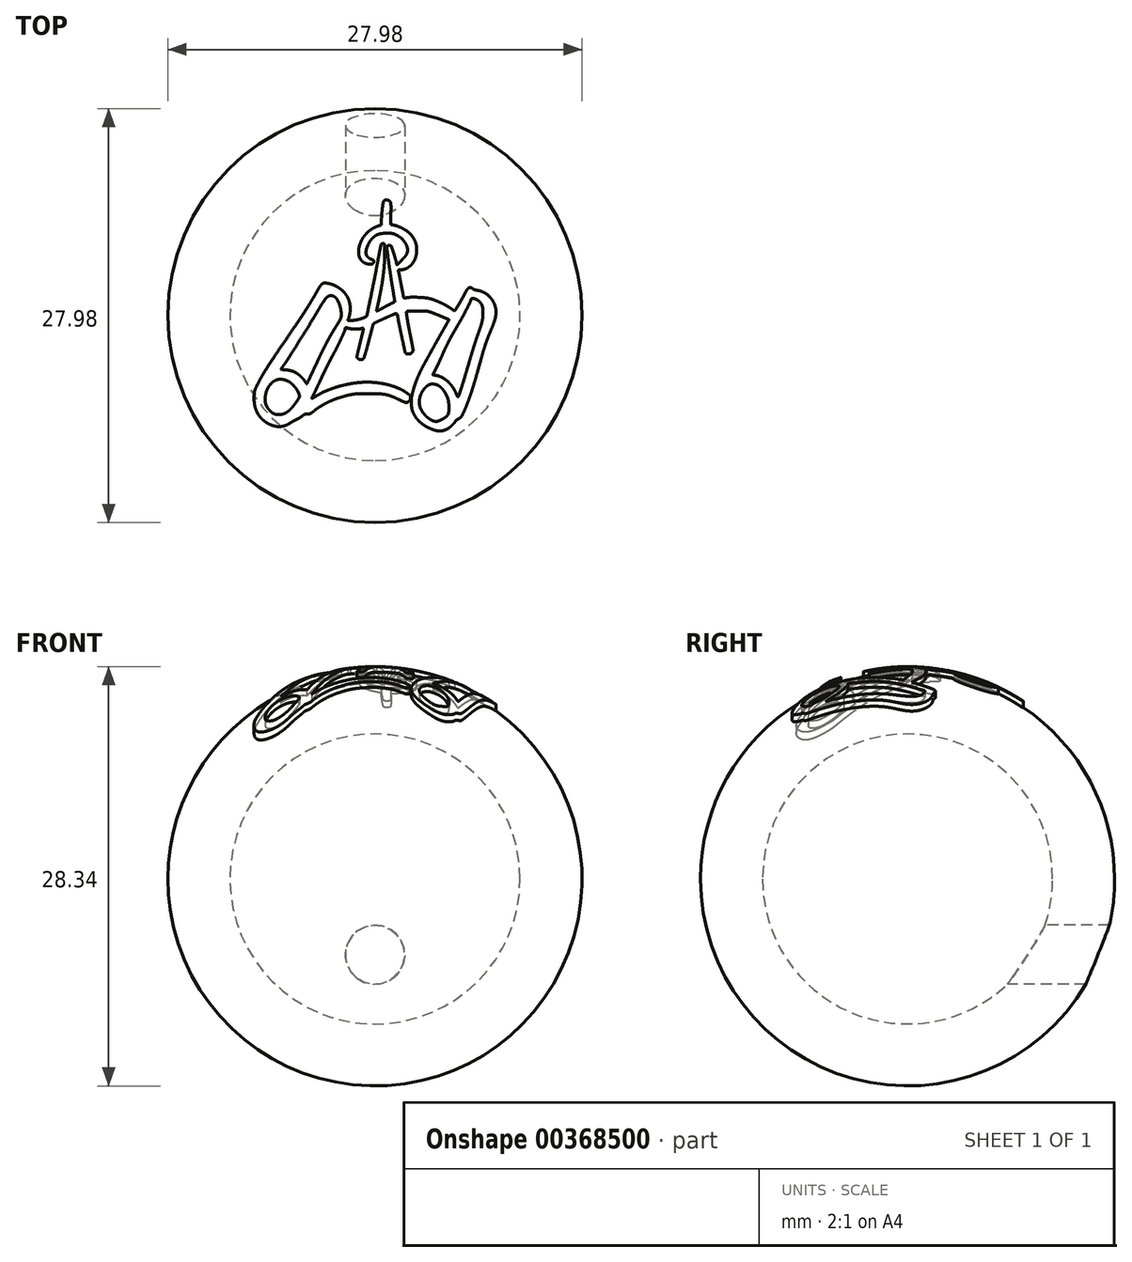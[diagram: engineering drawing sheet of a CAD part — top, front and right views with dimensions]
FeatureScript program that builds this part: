
annotation { "Feature Type Name" : "Feature", "Feature Type Description" : "" }
export const myFeature = defineFeature(function(context is Context, id is Id, definition is map)
    precondition{}
    {
        {
            var Q0;
            Q0=qCreatedBy(makeId("Top.planeOp"),FACE);
            var sketch = newSketch(context, id + "F0", { "sketchPlane" : qUnion([Q0])});
            skLineSegment(sketch, "E0", {"start": v(0, -10) * mm, "end": v(0, 10) * mm});
            skArc(sketch, "E1", {"start": v(0, 10) * mm, "mid": v(-10, 0) * mm, "end": v(0, -10) * mm});
            skSolve(sketch);
        }
        {
            var Q0;
            {var subQ0=sQuery(id+"F0.wireOp",EDGE,"E1");Q0=makeQuery(id+"F0.imprint","IMPRINT",FACE,{"disambiguationData":[TD([[makeQuery(id+"F0.imprint","IMPRINT",EDGE,{"derivedFrom":subQ0}),1.0]])]});}
            var Q1;
            Q1=sQuery(id+"F0.wireOp",EDGE,"E0");
            revolve(context, id + "F1", {"entities" : qUnion([Q0]), "axis" : qUnion([Q1]), "revolveType" : RevolveType.FULL});
        }
        {
            var Q0;
            Q0=makeQuery(id+"F1.opRevolve","SWEPT_BODY",BODY,{"disambiguationData":[OSD([sQuery(id+"F0.wireOp",EDGE,"E0"),sQuery(id+"F0.wireOp",EDGE,"E1")])]});
            var Q1;
            Q1=sQuery(id+"F0.wireOp",VERTEX,"NPe4G0ez-t7S9-9isL-QO5v-uuJu600mHcIT.center");
            var Q2;
            Q2=sQuery(id+"F0.wireOp",VERTEX,"E1.center");
            transform(context, id + "F2", {"entities" : qUnion([Q0]), "transformType" : TransformType.SCALE_UNIFORMLY, "scale" : 33.3, "scalePoint" : qUnion([Q2]), "makeCopy" : false});
        }
        {
            var Q0;
            Q0=qCreatedBy(makeId("Top.planeOp"),FACE);
            var sketch = newSketch(context, id + "F3", { "sketchPlane" : qUnion([Q0])});
            skArc(sketch, "E2", {"start": v(14.34, 184.46) * mm, "mid": v(13.65, 183.38) * mm, "end": v(13.25, 182.16) * mm});
            skArc(sketch, "E3", {"start": v(13.25, 182.16) * mm, "mid": v(12.71, 179.17) * mm, "end": v(12.25, 176.16) * mm});
            skArc(sketch, "E4", {"start": v(12.25, 176.16) * mm, "mid": v(11.73, 172.13) * mm, "end": v(11.32, 168.08) * mm});
            skArc(sketch, "E5", {"start": v(11.32, 168.08) * mm, "mid": v(10.9, 162.81) * mm, "end": v(10.53, 157.54) * mm});
            skLineSegment(sketch, "E6", {"start": v(10.53, 157.54) * mm, "end": v(9.8, 145.67) * mm});
            skLineSegment(sketch, "E7", {"start": v(9.8, 145.67) * mm, "end": v(3.78, 143.5) * mm});
            skArc(sketch, "E8", {"start": v(3.78, 143.5) * mm, "mid": v(-1.65, 141.13) * mm, "end": v(-6.72, 138.07) * mm});
            skArc(sketch, "E9", {"start": v(-6.72, 138.07) * mm, "mid": v(-11.38, 134.36) * mm, "end": v(-15.52, 130.08) * mm});
            skArc(sketch, "E10", {"start": v(-15.52, 130.08) * mm, "mid": v(-19.1, 125.3) * mm, "end": v(-22.03, 120.08) * mm});
            skArc(sketch, "E11", {"start": v(-22.03, 120.08) * mm, "mid": v(-24.3, 114.52) * mm, "end": v(-25.83, 108.72) * mm});
            skArc(sketch, "E12", {"start": v(-25.83, 108.72) * mm, "mid": v(-26.4, 104.16) * mm, "end": v(-26.28, 99.57) * mm});
            skArc(sketch, "E13", {"start": v(-26.28, 99.57) * mm, "mid": v(-25.48, 95.49) * mm, "end": v(-23.89, 91.65) * mm});
            skArc(sketch, "E14", {"start": v(-23.89, 91.65) * mm, "mid": v(-21.73, 88.51) * mm, "end": v(-18.93, 85.93) * mm});
            skArc(sketch, "E15", {"start": v(-18.93, 85.93) * mm, "mid": v(-15.67, 84.07) * mm, "end": v(-12.07, 83) * mm});
            skArc(sketch, "E16", {"start": v(-12.07, 83) * mm, "mid": v(-9.95, 82.7) * mm, "end": v(-7.82, 82.55) * mm});
            skArc(sketch, "E17", {"start": v(-7.82, 82.55) * mm, "mid": v(-6.26, 82.62) * mm, "end": v(-4.73, 82.96) * mm});
            skArc(sketch, "E18", {"start": v(-4.73, 82.96) * mm, "mid": v(-3.68, 83.44) * mm, "end": v(-2.8, 84.19) * mm});
            skArc(sketch, "E19", {"start": v(-2.8, 84.19) * mm, "mid": v(-2.19, 85.1) * mm, "end": v(-1.9, 86.15) * mm});
            skArc(sketch, "E20", {"start": v(-1.9, 86.15) * mm, "mid": v(-1.84, 86.88) * mm, "end": v(-1.86, 87.6) * mm});
            skArc(sketch, "E21", {"start": v(-1.86, 87.6) * mm, "mid": v(-1.96, 88.1) * mm, "end": v(-2.19, 88.56) * mm});
            skArc(sketch, "E22", {"start": v(-2.19, 88.56) * mm, "mid": v(-2.53, 88.96) * mm, "end": v(-2.96, 89.27) * mm});
            skArc(sketch, "E23", {"start": v(-2.96, 89.27) * mm, "mid": v(-3.66, 89.62) * mm, "end": v(-4.4, 89.92) * mm});
            skArc(sketch, "E24", {"start": v(-4.4, 89.92) * mm, "mid": v(-7.1, 91.04) * mm, "end": v(-9.71, 92.4) * mm});
            skArc(sketch, "E25", {"start": v(-9.71, 92.4) * mm, "mid": v(-11.45, 93.66) * mm, "end": v(-12.88, 95.27) * mm});
            skArc(sketch, "E26", {"start": v(-12.88, 95.27) * mm, "mid": v(-13.84, 97.04) * mm, "end": v(-14.34, 98.99) * mm});
            skArc(sketch, "E27", {"start": v(-14.34, 98.99) * mm, "mid": v(-14.52, 101.49) * mm, "end": v(-14.38, 104) * mm});
            skArc(sketch, "E28", {"start": v(-14.38, 104) * mm, "mid": v(-13.95, 106.46) * mm, "end": v(-13.24, 108.87) * mm});
            skArc(sketch, "E29", {"start": v(-13.24, 108.87) * mm, "mid": v(-12.08, 111.8) * mm, "end": v(-10.77, 114.65) * mm});
            skArc(sketch, "E30", {"start": v(-10.77, 114.65) * mm, "mid": v(-9.27, 117.46) * mm, "end": v(-7.61, 120.17) * mm});
            skArc(sketch, "E31", {"start": v(-7.61, 120.17) * mm, "mid": v(-6.07, 122.28) * mm, "end": v(-4.32, 124.22) * mm});
            skArc(sketch, "E32", {"start": v(-4.32, 124.22) * mm, "mid": v(-2.04, 126.3) * mm, "end": v(0.42, 128.16) * mm});
            skArc(sketch, "E33", {"start": v(0.42, 128.16) * mm, "mid": v(2.78, 129.56) * mm, "end": v(5.3, 130.64) * mm});
            skArc(sketch, "E34", {"start": v(5.3, 130.64) * mm, "mid": v(8.18, 131.48) * mm, "end": v(11.13, 131.98) * mm});
            skArc(sketch, "E35", {"start": v(11.13, 131.98) * mm, "mid": v(14.95, 132.3) * mm, "end": v(18.8, 132.4) * mm});
            skArc(sketch, "E36", {"start": v(18.8, 132.4) * mm, "mid": v(21.68, 132.38) * mm, "end": v(24.57, 132.3) * mm});
            skArc(sketch, "E37", {"start": v(24.57, 132.3) * mm, "mid": v(26.3, 132.18) * mm, "end": v(28.03, 131.95) * mm});
            skArc(sketch, "E38", {"start": v(28.03, 131.95) * mm, "mid": v(29.48, 131.62) * mm, "end": v(30.9, 131.17) * mm});
            skArc(sketch, "E39", {"start": v(30.9, 131.17) * mm, "mid": v(32.61, 130.47) * mm, "end": v(34.3, 129.7) * mm});
            skArc(sketch, "E40", {"start": v(34.3, 129.7) * mm, "mid": v(38, 127.6) * mm, "end": v(41.43, 125.08) * mm});
            skArc(sketch, "E41", {"start": v(41.43, 125.08) * mm, "mid": v(44.5, 122.2) * mm, "end": v(47.2, 118.99) * mm});
            skArc(sketch, "E42", {"start": v(47.2, 118.99) * mm, "mid": v(49.33, 115.7) * mm, "end": v(51, 112.16) * mm});
            skArc(sketch, "E43", {"start": v(51, 112.16) * mm, "mid": v(51.96, 108.85) * mm, "end": v(52.28, 105.42) * mm});
            skArc(sketch, "E44", {"start": v(52.28, 105.42) * mm, "mid": v(52.18, 103.4) * mm, "end": v(51.87, 101.4) * mm});
            skArc(sketch, "E45", {"start": v(51.87, 101.4) * mm, "mid": v(51.38, 99.73) * mm, "end": v(50.63, 98.17) * mm});
            skArc(sketch, "E46", {"start": v(50.63, 98.17) * mm, "mid": v(49.39, 96.27) * mm, "end": v(47.97, 94.5) * mm});
            skArc(sketch, "E47", {"start": v(47.97, 94.5) * mm, "mid": v(45.12, 91.31) * mm, "end": v(42.2, 88.18) * mm});
            skLineSegment(sketch, "E48", {"start": v(42.2, 88.18) * mm, "end": v(35.62, 81.22) * mm});
            skLineSegment(sketch, "E49", {"start": v(35.62, 81.22) * mm, "end": v(31.41, 95.8) * mm});
            skArc(sketch, "E50", {"start": v(31.41, 95.8) * mm, "mid": v(30.57, 98.66) * mm, "end": v(29.7, 101.5) * mm});
            skArc(sketch, "E51", {"start": v(29.7, 101.5) * mm, "mid": v(28.9, 104.02) * mm, "end": v(28.04, 106.52) * mm});
            skArc(sketch, "E52", {"start": v(28.04, 106.52) * mm, "mid": v(27.3, 108.6) * mm, "end": v(26.54, 110.68) * mm});
            skArc(sketch, "E53", {"start": v(26.54, 110.68) * mm, "mid": v(26.24, 111.27) * mm, "end": v(25.83, 111.78) * mm});
            skArc(sketch, "E54", {"start": v(25.83, 111.78) * mm, "mid": v(25.48, 112.08) * mm, "end": v(25.08, 112.32) * mm});
            skArc(sketch, "E55", {"start": v(25.08, 112.32) * mm, "mid": v(24.62, 112.5) * mm, "end": v(24.14, 112.63) * mm});
            skArc(sketch, "E56", {"start": v(24.14, 112.63) * mm, "mid": v(23.6, 112.7) * mm, "end": v(23.05, 112.7) * mm});
            skArc(sketch, "E57", {"start": v(23.05, 112.7) * mm, "mid": v(22.46, 112.63) * mm, "end": v(21.88, 112.51) * mm});
            skArc(sketch, "E58", {"start": v(21.88, 112.51) * mm, "mid": v(21.22, 112.3) * mm, "end": v(20.59, 112.04) * mm});
            skArc(sketch, "E59", {"start": v(20.59, 112.04) * mm, "mid": v(20.16, 111.77) * mm, "end": v(19.82, 111.4) * mm});
            skArc(sketch, "E60", {"start": v(19.82, 111.4) * mm, "mid": v(19.56, 110.94) * mm, "end": v(19.41, 110.43) * mm});
            skArc(sketch, "E61", {"start": v(19.41, 110.43) * mm, "mid": v(19.32, 109.68) * mm, "end": v(19.3, 108.93) * mm});
            skArc(sketch, "E62", {"start": v(19.3, 108.93) * mm, "mid": v(19.39, 106.06) * mm, "end": v(19.67, 103.2) * mm});
            skArc(sketch, "E63", {"start": v(19.67, 103.2) * mm, "mid": v(20.92, 93.82) * mm, "end": v(22.2, 84.45) * mm});
            skArc(sketch, "E64", {"start": v(22.2, 84.45) * mm, "mid": v(23.65, 74.23) * mm, "end": v(25.16, 64.02) * mm});
            skArc(sketch, "E65", {"start": v(25.16, 64.02) * mm, "mid": v(26.64, 54.39) * mm, "end": v(28.18, 44.76) * mm});
            skLineSegment(sketch, "E66", {"start": v(28.18, 44.76) * mm, "end": v(31.9, 22.13) * mm});
            skLineSegment(sketch, "E67", {"start": v(31.9, 22.13) * mm, "end": v(26.35, 19.42) * mm});
            skArc(sketch, "E68", {"start": v(26.35, 19.42) * mm, "mid": v(24.97, 18.74) * mm, "end": v(23.6, 18.04) * mm});
            skArc(sketch, "E69", {"start": v(23.6, 18.04) * mm, "mid": v(21.71, 17.05) * mm, "end": v(19.82, 16.05) * mm});
            skArc(sketch, "E70", {"start": v(19.82, 16.05) * mm, "mid": v(17.78, 14.95) * mm, "end": v(15.74, 13.84) * mm});
            skArc(sketch, "E71", {"start": v(15.74, 13.84) * mm, "mid": v(13.84, 12.8) * mm, "end": v(11.94, 11.74) * mm});
            skArc(sketch, "E72", {"start": v(11.94, 11.74) * mm, "mid": v(10.24, 10.8) * mm, "end": v(8.52, 9.86) * mm});
            skArc(sketch, "E73", {"start": v(8.52, 9.86) * mm, "mid": v(7.06, 9.08) * mm, "end": v(5.59, 8.33) * mm});
            skArc(sketch, "E74", {"start": v(5.59, 8.33) * mm, "mid": v(4.32, 7.7) * mm, "end": v(3.04, 7.07) * mm});
            skArc(sketch, "E75", {"start": v(3.04, 7.07) * mm, "mid": v(2.88, 7.04) * mm, "end": v(2.74, 7.12) * mm});
            skArc(sketch, "E76", {"start": v(2.74, 7.12) * mm, "mid": v(2.65, 7.27) * mm, "end": v(2.64, 7.44) * mm});
            skArc(sketch, "E77", {"start": v(2.64, 7.44) * mm, "mid": v(2.93, 9.01) * mm, "end": v(3.22, 10.58) * mm});
            skArc(sketch, "E78", {"start": v(3.22, 10.58) * mm, "mid": v(3.57, 12.38) * mm, "end": v(3.94, 14.18) * mm});
            skArc(sketch, "E79", {"start": v(3.94, 14.18) * mm, "mid": v(4.4, 16.3) * mm, "end": v(4.86, 18.4) * mm});
            skArc(sketch, "E80", {"start": v(4.86, 18.4) * mm, "mid": v(7.3, 29.7) * mm, "end": v(9.54, 41.06) * mm});
            skArc(sketch, "E81", {"start": v(9.54, 41.06) * mm, "mid": v(11.33, 51.39) * mm, "end": v(12.86, 61.75) * mm});
            skArc(sketch, "E82", {"start": v(12.86, 61.75) * mm, "mid": v(14.01, 71.25) * mm, "end": v(14.9, 80.77) * mm});
            skArc(sketch, "E83", {"start": v(14.9, 80.77) * mm, "mid": v(15.43, 89.58) * mm, "end": v(15.66, 98.4) * mm});
            skArc(sketch, "E84", {"start": v(15.66, 98.4) * mm, "mid": v(15.69, 103.78) * mm, "end": v(15.7, 109.17) * mm});
            skArc(sketch, "E85", {"start": v(15.7, 109.17) * mm, "mid": v(15.65, 111.11) * mm, "end": v(15.5, 113.05) * mm});
            skArc(sketch, "E86", {"start": v(15.5, 113.05) * mm, "mid": v(15.3, 114) * mm, "end": v(14.92, 114.88) * mm});
            skArc(sketch, "E87", {"start": v(14.92, 114.88) * mm, "mid": v(14.45, 115.4) * mm, "end": v(13.8, 115.66) * mm});
            skArc(sketch, "E88", {"start": v(13.8, 115.66) * mm, "mid": v(13.36, 115.7) * mm, "end": v(12.93, 115.7) * mm});
            skArc(sketch, "E89", {"start": v(12.93, 115.7) * mm, "mid": v(12.47, 115.66) * mm, "end": v(12.01, 115.6) * mm});
            skArc(sketch, "E90", {"start": v(12.01, 115.6) * mm, "mid": v(11.59, 115.51) * mm, "end": v(11.17, 115.4) * mm});
            skArc(sketch, "E91", {"start": v(11.17, 115.4) * mm, "mid": v(10.85, 115.27) * mm, "end": v(10.55, 115.1) * mm});
            skArc(sketch, "E92", {"start": v(10.55, 115.1) * mm, "mid": v(10.18, 114.74) * mm, "end": v(9.96, 114.27) * mm});
            skArc(sketch, "E93", {"start": v(9.96, 114.27) * mm, "mid": v(9.3, 111.54) * mm, "end": v(8.66, 108.8) * mm});
            skArc(sketch, "E94", {"start": v(8.66, 108.8) * mm, "mid": v(7.93, 105.55) * mm, "end": v(7.26, 102.3) * mm});
            skArc(sketch, "E95", {"start": v(7.26, 102.3) * mm, "mid": v(6.52, 98.49) * mm, "end": v(5.83, 94.68) * mm});
            skArc(sketch, "E96", {"start": v(5.83, 94.68) * mm, "mid": v(3.24, 80.45) * mm, "end": v(0.53, 66.24) * mm});
            skArc(sketch, "E97", {"start": v(0.53, 66.24) * mm, "mid": v(-2.7, 49.95) * mm, "end": v(-6.01, 33.68) * mm});
            skArc(sketch, "E98", {"start": v(-6.01, 33.68) * mm, "mid": v(-9.46, 17.03) * mm, "end": v(-12.92, 0.37) * mm});
            skArc(sketch, "E99", {"start": v(-12.92, 0.37) * mm, "mid": v(-13.36, -0.82) * mm, "end": v(-14.12, -1.85) * mm});
            skArc(sketch, "E100", {"start": v(-14.12, -1.85) * mm, "mid": v(-14.3, -2) * mm, "end": v(-14.5, -2.1) * mm});
            skArc(sketch, "E101", {"start": v(-14.5, -2.1) * mm, "mid": v(-15.47, -2.5) * mm, "end": v(-16.44, -2.9) * mm});
            skArc(sketch, "E102", {"start": v(-16.44, -2.9) * mm, "mid": v(-17.6, -3.36) * mm, "end": v(-18.75, -3.8) * mm});
            skArc(sketch, "E103", {"start": v(-18.75, -3.8) * mm, "mid": v(-20.07, -4.3) * mm, "end": v(-21.4, -4.8) * mm});
            skArc(sketch, "E104", {"start": v(-21.4, -4.8) * mm, "mid": v(-24.7, -5.86) * mm, "end": v(-28.07, -6.69) * mm});
            skArc(sketch, "E105", {"start": v(-28.07, -6.69) * mm, "mid": v(-31.93, -7.38) * mm, "end": v(-35.82, -7.87) * mm});
            skArc(sketch, "E106", {"start": v(-35.82, -7.87) * mm, "mid": v(-39.17, -8.14) * mm, "end": v(-42.54, -8.26) * mm});
            skArc(sketch, "E107", {"start": v(-42.54, -8.26) * mm, "mid": v(-43.31, -7.86) * mm, "end": v(-43.4, -7) * mm});
            skArc(sketch, "E108", {"start": v(-43.4, -7) * mm, "mid": v(-41.81, -2.55) * mm, "end": v(-40.64, 2.04) * mm});
            skArc(sketch, "E109", {"start": v(-40.64, 2.04) * mm, "mid": v(-39.95, 6.54) * mm, "end": v(-39.73, 11.1) * mm});
            skArc(sketch, "E110", {"start": v(-39.73, 11.1) * mm, "mid": v(-39.97, 15.5) * mm, "end": v(-40.7, 19.84) * mm});
            skArc(sketch, "E111", {"start": v(-40.7, 19.84) * mm, "mid": v(-41.86, 23.99) * mm, "end": v(-43.5, 27.97) * mm});
            skArc(sketch, "E112", {"start": v(-43.5, 27.97) * mm, "mid": v(-45.84, 32.18) * mm, "end": v(-48.67, 36.07) * mm});
            skArc(sketch, "E113", {"start": v(-48.67, 36.07) * mm, "mid": v(-52.02, 39.68) * mm, "end": v(-55.77, 42.88) * mm});
            skArc(sketch, "E114", {"start": v(-55.77, 42.88) * mm, "mid": v(-59.97, 45.73) * mm, "end": v(-64.46, 48.1) * mm});
            skArc(sketch, "E115", {"start": v(-64.46, 48.1) * mm, "mid": v(-69.32, 50.03) * mm, "end": v(-74.35, 51.47) * mm});
            skArc(sketch, "E116", {"start": v(-74.35, 51.47) * mm, "mid": v(-77.6, 52.06) * mm, "end": v(-80.88, 52.34) * mm});
            skArc(sketch, "E117", {"start": v(-80.88, 52.34) * mm, "mid": v(-82.95, 52.05) * mm, "end": v(-84.8, 51.08) * mm});
            skArc(sketch, "E118", {"start": v(-84.8, 51.08) * mm, "mid": v(-86.77, 49.23) * mm, "end": v(-88.38, 47.06) * mm});
            skArc(sketch, "E119", {"start": v(-88.38, 47.06) * mm, "mid": v(-91.9, 41.16) * mm, "end": v(-95.34, 35.2) * mm});
            skArc(sketch, "E120", {"start": v(-95.34, 35.2) * mm, "mid": v(-99.5, 28.01) * mm, "end": v(-103.77, 20.9) * mm});
            skArc(sketch, "E121", {"start": v(-103.77, 20.9) * mm, "mid": v(-108.75, 12.9) * mm, "end": v(-113.83, 4.98) * mm});
            skArc(sketch, "E122", {"start": v(-113.83, 4.98) * mm, "mid": v(-120.33, -4.92) * mm, "end": v(-126.92, -14.75) * mm});
            skArc(sketch, "E123", {"start": v(-126.92, -14.75) * mm, "mid": v(-135.97, -28.08) * mm, "end": v(-145.08, -41.37) * mm});
            skArc(sketch, "E124", {"start": v(-145.08, -41.37) * mm, "mid": v(-153.2, -53.26) * mm, "end": v(-161.26, -65.2) * mm});
            skArc(sketch, "E125", {"start": v(-161.26, -65.2) * mm, "mid": v(-167.24, -74.22) * mm, "end": v(-173.1, -83.34) * mm});
            skArc(sketch, "E126", {"start": v(-173.1, -83.34) * mm, "mid": v(-177.56, -90.54) * mm, "end": v(-181.9, -97.82) * mm});
            skArc(sketch, "E127", {"start": v(-181.9, -97.82) * mm, "mid": v(-185.29, -103.81) * mm, "end": v(-188.47, -109.91) * mm});
            skArc(sketch, "E128", {"start": v(-188.47, -109.91) * mm, "mid": v(-190.25, -113.53) * mm, "end": v(-192, -117.16) * mm});
            skArc(sketch, "E129", {"start": v(-192, -117.16) * mm, "mid": v(-192.8, -119.06) * mm, "end": v(-193.44, -121.02) * mm});
            skArc(sketch, "E130", {"start": v(-193.44, -121.02) * mm, "mid": v(-193.88, -122.88) * mm, "end": v(-194.14, -124.77) * mm});
            skArc(sketch, "E131", {"start": v(-194.14, -124.77) * mm, "mid": v(-194.37, -127.9) * mm, "end": v(-194.54, -131.03) * mm});
            skArc(sketch, "E132", {"start": v(-194.54, -131.03) * mm, "mid": v(-194.38, -138.24) * mm, "end": v(-193.34, -145.39) * mm});
            skArc(sketch, "E133", {"start": v(-193.34, -145.39) * mm, "mid": v(-191.48, -151.78) * mm, "end": v(-188.63, -157.8) * mm});
            skArc(sketch, "E134", {"start": v(-188.63, -157.8) * mm, "mid": v(-184.97, -163.14) * mm, "end": v(-180.5, -167.83) * mm});
            skArc(sketch, "E135", {"start": v(-180.5, -167.83) * mm, "mid": v(-175.16, -171.93) * mm, "end": v(-169.28, -175.21) * mm});
            skArc(sketch, "E136", {"start": v(-169.28, -175.21) * mm, "mid": v(-165, -176.93) * mm, "end": v(-160.56, -178.16) * mm});
            skArc(sketch, "E137", {"start": v(-160.56, -178.16) * mm, "mid": v(-156.38, -178.75) * mm, "end": v(-152.16, -178.74) * mm});
            skArc(sketch, "E138", {"start": v(-152.16, -178.74) * mm, "mid": v(-147.99, -178.12) * mm, "end": v(-143.95, -176.9) * mm});
            skArc(sketch, "E139", {"start": v(-143.95, -176.9) * mm, "mid": v(-139.78, -175.02) * mm, "end": v(-135.84, -172.69) * mm});
            skArc(sketch, "E140", {"start": v(-135.84, -172.69) * mm, "mid": v(-134.67, -171.92) * mm, "end": v(-133.48, -171.19) * mm});
            skArc(sketch, "E141", {"start": v(-133.48, -171.19) * mm, "mid": v(-132.02, -170.33) * mm, "end": v(-130.56, -169.5) * mm});
            skArc(sketch, "E142", {"start": v(-130.56, -169.5) * mm, "mid": v(-129.07, -168.68) * mm, "end": v(-127.57, -167.89) * mm});
            skArc(sketch, "E143", {"start": v(-127.57, -167.89) * mm, "mid": v(-126.28, -167.24) * mm, "end": v(-124.99, -166.63) * mm});
            skArc(sketch, "E144", {"start": v(-124.99, -166.63) * mm, "mid": v(-123.77, -166.04) * mm, "end": v(-122.57, -165.42) * mm});
            skArc(sketch, "E145", {"start": v(-122.57, -165.42) * mm, "mid": v(-121.31, -164.71) * mm, "end": v(-120.08, -163.97) * mm});
            skArc(sketch, "E146", {"start": v(-120.08, -163.97) * mm, "mid": v(-118.96, -163.26) * mm, "end": v(-117.87, -162.51) * mm});
            skArc(sketch, "E147", {"start": v(-117.87, -162.51) * mm, "mid": v(-117.11, -161.93) * mm, "end": v(-116.4, -161.3) * mm});
            skArc(sketch, "E148", {"start": v(-116.4, -161.3) * mm, "mid": v(-115.6, -160.59) * mm, "end": v(-114.75, -159.94) * mm});
            skArc(sketch, "E149", {"start": v(-114.75, -159.94) * mm, "mid": v(-114, -159.49) * mm, "end": v(-113.2, -159.14) * mm});
            skArc(sketch, "E150", {"start": v(-113.2, -159.14) * mm, "mid": v(-112.29, -158.88) * mm, "end": v(-111.36, -158.73) * mm});
            skArc(sketch, "E151", {"start": v(-111.36, -158.73) * mm, "mid": v(-110.1, -158.63) * mm, "end": v(-108.83, -158.6) * mm});
            skArc(sketch, "E152", {"start": v(-108.83, -158.6) * mm, "mid": v(-107.46, -158.56) * mm, "end": v(-106.1, -158.42) * mm});
            skArc(sketch, "E153", {"start": v(-106.1, -158.42) * mm, "mid": v(-105.05, -158.22) * mm, "end": v(-104.05, -157.87) * mm});
            skArc(sketch, "E154", {"start": v(-104.05, -157.87) * mm, "mid": v(-103, -157.36) * mm, "end": v(-102, -156.73) * mm});
            skArc(sketch, "E155", {"start": v(-102, -156.73) * mm, "mid": v(-100.56, -155.65) * mm, "end": v(-99.15, -154.52) * mm});
            skArc(sketch, "E156", {"start": v(-99.15, -154.52) * mm, "mid": v(-93.2, -149.94) * mm, "end": v(-86.94, -145.77) * mm});
            skArc(sketch, "E157", {"start": v(-86.94, -145.77) * mm, "mid": v(-80.24, -141.9) * mm, "end": v(-73.3, -138.46) * mm});
            skArc(sketch, "E158", {"start": v(-73.3, -138.46) * mm, "mid": v(-65.76, -135.26) * mm, "end": v(-58.04, -132.51) * mm});
            skArc(sketch, "E159", {"start": v(-58.04, -132.51) * mm, "mid": v(-49.56, -129.99) * mm, "end": v(-40.97, -127.85) * mm});
            skArc(sketch, "E160", {"start": v(-40.97, -127.85) * mm, "mid": v(-37.92, -127.23) * mm, "end": v(-34.86, -126.7) * mm});
            skArc(sketch, "E161", {"start": v(-34.86, -126.7) * mm, "mid": v(-32, -126.32) * mm, "end": v(-29.13, -126.06) * mm});
            skArc(sketch, "E162", {"start": v(-29.13, -126.06) * mm, "mid": v(-25.47, -125.86) * mm, "end": v(-21.81, -125.76) * mm});
            skArc(sketch, "E163", {"start": v(-21.81, -125.76) * mm, "mid": v(-15.76, -125.7) * mm, "end": v(-9.7, -125.7) * mm});
            skArc(sketch, "E164", {"start": v(-9.7, -125.7) * mm, "mid": v(-1.4, -125.79) * mm, "end": v(6.9, -126.06) * mm});
            skArc(sketch, "E165", {"start": v(6.9, -126.06) * mm, "mid": v(12.17, -126.49) * mm, "end": v(17.4, -127.32) * mm});
            skArc(sketch, "E166", {"start": v(17.4, -127.32) * mm, "mid": v(22.02, -128.45) * mm, "end": v(26.52, -130) * mm});
            skArc(sketch, "E167", {"start": v(26.52, -130) * mm, "mid": v(32.23, -132.42) * mm, "end": v(37.83, -135.08) * mm});
            skArc(sketch, "E168", {"start": v(37.83, -135.08) * mm, "mid": v(39.82, -136.05) * mm, "end": v(41.82, -137) * mm});
            skArc(sketch, "E169", {"start": v(41.82, -137) * mm, "mid": v(43.67, -137.83) * mm, "end": v(45.53, -138.62) * mm});
            skArc(sketch, "E170", {"start": v(45.53, -138.62) * mm, "mid": v(47.09, -139.26) * mm, "end": v(48.65, -139.86) * mm});
            skArc(sketch, "E171", {"start": v(48.65, -139.86) * mm, "mid": v(49.29, -140.04) * mm, "end": v(49.94, -140.1) * mm});
            skArc(sketch, "E172", {"start": v(49.94, -140.1) * mm, "mid": v(51.3, -139.95) * mm, "end": v(52.6, -139.5) * mm});
            skArc(sketch, "E173", {"start": v(52.6, -139.5) * mm, "mid": v(53.87, -138.72) * mm, "end": v(55, -137.74) * mm});
            skArc(sketch, "E174", {"start": v(55, -137.74) * mm, "mid": v(55.96, -136.58) * mm, "end": v(56.7, -135.26) * mm});
            skArc(sketch, "E175", {"start": v(56.7, -135.26) * mm, "mid": v(57.14, -133.93) * mm, "end": v(57.3, -132.54) * mm});
            skArc(sketch, "E176", {"start": v(57.3, -132.54) * mm, "mid": v(57.24, -131.55) * mm, "end": v(57.08, -130.58) * mm});
            skArc(sketch, "E177", {"start": v(57.08, -130.58) * mm, "mid": v(56.83, -129.8) * mm, "end": v(56.44, -129.1) * mm});
            skArc(sketch, "E178", {"start": v(56.44, -129.1) * mm, "mid": v(55.82, -128.32) * mm, "end": v(55.11, -127.63) * mm});
            skArc(sketch, "E179", {"start": v(55.11, -127.63) * mm, "mid": v(53.84, -126.59) * mm, "end": v(52.54, -125.59) * mm});
            skArc(sketch, "E180", {"start": v(52.54, -125.59) * mm, "mid": v(47.48, -122.16) * mm, "end": v(42.12, -119.2) * mm});
            skArc(sketch, "E181", {"start": v(42.12, -119.2) * mm, "mid": v(35.97, -116.42) * mm, "end": v(29.64, -114.04) * mm});
            skArc(sketch, "E182", {"start": v(29.64, -114.04) * mm, "mid": v(22.62, -111.91) * mm, "end": v(15.48, -110.22) * mm});
            skArc(sketch, "E183", {"start": v(15.48, -110.22) * mm, "mid": v(7.8, -108.85) * mm, "end": v(0.07, -107.87) * mm});
            skArc(sketch, "E184", {"start": v(0.07, -107.87) * mm, "mid": v(-11.56, -107.24) * mm, "end": v(-23.2, -107.67) * mm});
            skArc(sketch, "E185", {"start": v(-23.2, -107.67) * mm, "mid": v(-35.8, -109.16) * mm, "end": v(-48.27, -111.52) * mm});
            skArc(sketch, "E186", {"start": v(-48.27, -111.52) * mm, "mid": v(-60.58, -114.77) * mm, "end": v(-72.63, -118.87) * mm});
            skArc(sketch, "E187", {"start": v(-72.63, -118.87) * mm, "mid": v(-83.4, -123.52) * mm, "end": v(-93.73, -129.11) * mm});
            skArc(sketch, "E188", {"start": v(-93.73, -129.11) * mm, "mid": v(-95.26, -130.02) * mm, "end": v(-96.8, -130.92) * mm});
            skArc(sketch, "E189", {"start": v(-96.8, -130.92) * mm, "mid": v(-98.07, -131.66) * mm, "end": v(-99.37, -132.37) * mm});
            skArc(sketch, "E190", {"start": v(-99.37, -132.37) * mm, "mid": v(-100.46, -132.97) * mm, "end": v(-101.56, -133.57) * mm});
            skArc(sketch, "E191", {"start": v(-101.56, -133.57) * mm, "mid": v(-101.66, -133.57) * mm, "end": v(-101.7, -133.48) * mm});
            skArc(sketch, "E192", {"start": v(-101.7, -133.48) * mm, "mid": v(-101.7, -133.32) * mm, "end": v(-101.64, -133.17) * mm});
            skArc(sketch, "E193", {"start": v(-101.64, -133.17) * mm, "mid": v(-101.08, -131.99) * mm, "end": v(-100.52, -130.8) * mm});
            skArc(sketch, "E194", {"start": v(-100.52, -130.8) * mm, "mid": v(-99.86, -129.45) * mm, "end": v(-99.2, -128.1) * mm});
            skArc(sketch, "E195", {"start": v(-99.2, -128.1) * mm, "mid": v(-98.43, -126.54) * mm, "end": v(-97.65, -124.98) * mm});
            skArc(sketch, "E196", {"start": v(-97.65, -124.98) * mm, "mid": v(-96.6, -122.86) * mm, "end": v(-95.56, -120.72) * mm});
            skArc(sketch, "E197", {"start": v(-95.56, -120.72) * mm, "mid": v(-94, -117.43) * mm, "end": v(-92.45, -114.14) * mm});
            skArc(sketch, "E198", {"start": v(-92.45, -114.14) * mm, "mid": v(-90.72, -110.43) * mm, "end": v(-89, -106.7) * mm});
            skArc(sketch, "E199", {"start": v(-89, -106.7) * mm, "mid": v(-87.32, -103.07) * mm, "end": v(-85.66, -99.43) * mm});
            skArc(sketch, "E200", {"start": v(-85.66, -99.43) * mm, "mid": v(-83.79, -95.37) * mm, "end": v(-81.86, -91.34) * mm});
            skArc(sketch, "E201", {"start": v(-81.86, -91.34) * mm, "mid": v(-79.41, -86.34) * mm, "end": v(-76.93, -81.36) * mm});
            skArc(sketch, "E202", {"start": v(-76.93, -81.36) * mm, "mid": v(-74.35, -76.27) * mm, "end": v(-71.74, -71.2) * mm});
            skArc(sketch, "E203", {"start": v(-71.74, -71.2) * mm, "mid": v(-69.44, -66.8) * mm, "end": v(-67.1, -62.45) * mm});
            skArc(sketch, "E204", {"start": v(-67.1, -62.45) * mm, "mid": v(-63.55, -55.84) * mm, "end": v(-60.13, -49.17) * mm});
            skArc(sketch, "E205", {"start": v(-60.13, -49.17) * mm, "mid": v(-56.9, -42.6) * mm, "end": v(-53.78, -35.96) * mm});
            skArc(sketch, "E206", {"start": v(-53.78, -35.96) * mm, "mid": v(-51.14, -30.12) * mm, "end": v(-48.56, -24.25) * mm});
            skArc(sketch, "E207", {"start": v(-48.56, -24.25) * mm, "mid": v(-47.94, -22.29) * mm, "end": v(-47.72, -20.24) * mm});
            skArc(sketch, "E208", {"start": v(-47.72, -20.24) * mm, "mid": v(-47.69, -19.98) * mm, "end": v(-47.6, -19.73) * mm});
            skArc(sketch, "E209", {"start": v(-47.6, -19.73) * mm, "mid": v(-47.46, -19.54) * mm, "end": v(-47.28, -19.42) * mm});
            skArc(sketch, "E210", {"start": v(-47.28, -19.42) * mm, "mid": v(-47.02, -19.34) * mm, "end": v(-46.76, -19.34) * mm});
            skArc(sketch, "E211", {"start": v(-46.76, -19.34) * mm, "mid": v(-46.41, -19.4) * mm, "end": v(-46.08, -19.51) * mm});
            skArc(sketch, "E212", {"start": v(-46.08, -19.51) * mm, "mid": v(-43.19, -20.46) * mm, "end": v(-40.21, -21.12) * mm});
            skArc(sketch, "E213", {"start": v(-40.21, -21.12) * mm, "mid": v(-36.72, -21.6) * mm, "end": v(-33.21, -21.85) * mm});
            skArc(sketch, "E214", {"start": v(-33.21, -21.85) * mm, "mid": v(-29.67, -21.87) * mm, "end": v(-26.14, -21.67) * mm});
            skArc(sketch, "E215", {"start": v(-26.14, -21.67) * mm, "mid": v(-23.07, -21.25) * mm, "end": v(-20.05, -20.53) * mm});
            skArc(sketch, "E216", {"start": v(-20.05, -20.53) * mm, "mid": v(-19.45, -20.61) * mm, "end": v(-19.08, -21.1) * mm});
            skArc(sketch, "E217", {"start": v(-19.08, -21.1) * mm, "mid": v(-18.94, -22.16) * mm, "end": v(-19, -23.23) * mm});
            skArc(sketch, "E218", {"start": v(-19, -23.23) * mm, "mid": v(-19.47, -25.76) * mm, "end": v(-20.03, -28.26) * mm});
            skArc(sketch, "E219", {"start": v(-20.03, -28.26) * mm, "mid": v(-21.82, -35.52) * mm, "end": v(-23.63, -42.78) * mm});
            skArc(sketch, "E220", {"start": v(-23.63, -42.78) * mm, "mid": v(-24.72, -47.21) * mm, "end": v(-25.8, -51.65) * mm});
            skArc(sketch, "E221", {"start": v(-25.8, -51.65) * mm, "mid": v(-26.69, -55.5) * mm, "end": v(-27.55, -59.36) * mm});
            skArc(sketch, "E222", {"start": v(-27.55, -59.36) * mm, "mid": v(-28.26, -62.68) * mm, "end": v(-28.97, -66) * mm});
            skArc(sketch, "E223", {"start": v(-28.97, -66) * mm, "mid": v(-29.01, -66.56) * mm, "end": v(-28.92, -67.12) * mm});
            skArc(sketch, "E224", {"start": v(-28.92, -67.12) * mm, "mid": v(-28.28, -68.45) * mm, "end": v(-27.27, -69.52) * mm});
            skArc(sketch, "E225", {"start": v(-27.27, -69.52) * mm, "mid": v(-25.86, -70.38) * mm, "end": v(-24.29, -70.9) * mm});
            skArc(sketch, "E226", {"start": v(-24.29, -70.9) * mm, "mid": v(-22.64, -71.06) * mm, "end": v(-21, -70.86) * mm});
            skArc(sketch, "E227", {"start": v(-21, -70.86) * mm, "mid": v(-19.62, -70.3) * mm, "end": v(-18.48, -69.35) * mm});
            skArc(sketch, "E228", {"start": v(-18.48, -69.35) * mm, "mid": v(-18, -68.67) * mm, "end": v(-17.66, -67.9) * mm});
            skArc(sketch, "E229", {"start": v(-17.66, -67.9) * mm, "mid": v(-16.54, -64.27) * mm, "end": v(-15.43, -60.62) * mm});
            skArc(sketch, "E230", {"start": v(-15.43, -60.62) * mm, "mid": v(-14.16, -56.32) * mm, "end": v(-12.94, -52) * mm});
            skArc(sketch, "E231", {"start": v(-12.94, -52) * mm, "mid": v(-11.59, -47.05) * mm, "end": v(-10.28, -42.1) * mm});
            skArc(sketch, "E232", {"start": v(-10.28, -42.1) * mm, "mid": v(-8.98, -37.15) * mm, "end": v(-7.68, -32.2) * mm});
            skArc(sketch, "E233", {"start": v(-7.68, -32.2) * mm, "mid": v(-6.55, -27.87) * mm, "end": v(-5.41, -23.54) * mm});
            skArc(sketch, "E234", {"start": v(-5.41, -23.54) * mm, "mid": v(-4.43, -19.83) * mm, "end": v(-3.45, -16.13) * mm});
            skArc(sketch, "E235", {"start": v(-3.45, -16.13) * mm, "mid": v(-3.26, -15.43) * mm, "end": v(-3.06, -14.74) * mm});
            skArc(sketch, "E236", {"start": v(-3.06, -14.74) * mm, "mid": v(-2.13, -13.04) * mm, "end": v(-0.59, -11.86) * mm});
            skArc(sketch, "E237", {"start": v(-0.59, -11.86) * mm, "mid": v(7.47, -8.13) * mm, "end": v(15.57, -4.48) * mm});
            skArc(sketch, "E238", {"start": v(15.57, -4.48) * mm, "mid": v(23.74, -0.89) * mm, "end": v(31.95, 2.62) * mm});
            skArc(sketch, "E239", {"start": v(31.95, 2.62) * mm, "mid": v(33.7, 2.9) * mm, "end": v(35.37, 2.35) * mm});
            skArc(sketch, "E240", {"start": v(35.37, 2.35) * mm, "mid": v(35.56, 2.18) * mm, "end": v(35.67, 1.96) * mm});
            skArc(sketch, "E241", {"start": v(35.67, 1.96) * mm, "mid": v(35.88, 1.31) * mm, "end": v(36.06, 0.65) * mm});
            skArc(sketch, "E242", {"start": v(36.06, 0.65) * mm, "mid": v(36.26, -0.16) * mm, "end": v(36.44, -0.98) * mm});
            skArc(sketch, "E243", {"start": v(36.44, -0.98) * mm, "mid": v(36.6, -1.9) * mm, "end": v(36.75, -2.84) * mm});
            skArc(sketch, "E244", {"start": v(36.75, -2.84) * mm, "mid": v(37.64, -8.37) * mm, "end": v(38.7, -13.88) * mm});
            skArc(sketch, "E245", {"start": v(38.7, -13.88) * mm, "mid": v(40.96, -24.57) * mm, "end": v(43.27, -35.24) * mm});
            skArc(sketch, "E246", {"start": v(43.27, -35.24) * mm, "mid": v(45.85, -47) * mm, "end": v(48.44, -58.74) * mm});
            skArc(sketch, "E247", {"start": v(48.44, -58.74) * mm, "mid": v(48.81, -59.8) * mm, "end": v(49.43, -60.76) * mm});
            skArc(sketch, "E248", {"start": v(49.43, -60.76) * mm, "mid": v(50.25, -61.48) * mm, "end": v(51.26, -61.9) * mm});
            skArc(sketch, "E249", {"start": v(51.26, -61.9) * mm, "mid": v(52.64, -62.1) * mm, "end": v(54.03, -62.07) * mm});
            skArc(sketch, "E250", {"start": v(54.03, -62.07) * mm, "mid": v(55.5, -61.8) * mm, "end": v(56.92, -61.32) * mm});
            skArc(sketch, "E251", {"start": v(56.92, -61.32) * mm, "mid": v(58.1, -60.67) * mm, "end": v(59.12, -59.79) * mm});
            skArc(sketch, "E252", {"start": v(59.12, -59.79) * mm, "mid": v(59.55, -59.3) * mm, "end": v(59.95, -58.77) * mm});
            skArc(sketch, "E253", {"start": v(59.95, -58.77) * mm, "mid": v(60.32, -58.21) * mm, "end": v(60.65, -57.63) * mm});
            skArc(sketch, "E254", {"start": v(60.65, -57.63) * mm, "mid": v(60.92, -57.1) * mm, "end": v(61.14, -56.55) * mm});
            skArc(sketch, "E255", {"start": v(61.14, -56.55) * mm, "mid": v(61.25, -56.14) * mm, "end": v(61.3, -55.71) * mm});
            skArc(sketch, "E256", {"start": v(61.3, -55.71) * mm, "mid": v(61.26, -55.09) * mm, "end": v(61.18, -54.47) * mm});
            skArc(sketch, "E257", {"start": v(61.18, -54.47) * mm, "mid": v(60.74, -52.02) * mm, "end": v(60.3, -49.57) * mm});
            skArc(sketch, "E258", {"start": v(60.3, -49.57) * mm, "mid": v(59.75, -46.68) * mm, "end": v(59.19, -43.8) * mm});
            skArc(sketch, "E259", {"start": v(59.19, -43.8) * mm, "mid": v(58.54, -40.53) * mm, "end": v(57.88, -37.28) * mm});
            skArc(sketch, "E260", {"start": v(57.88, -37.28) * mm, "mid": v(55.91, -27.49) * mm, "end": v(54, -17.7) * mm});
            skArc(sketch, "E261", {"start": v(54, -17.7) * mm, "mid": v(52.83, -11.3) * mm, "end": v(51.78, -4.89) * mm});
            skArc(sketch, "E262", {"start": v(51.78, -4.89) * mm, "mid": v(51.12, -0.35) * mm, "end": v(50.51, 4.2) * mm});
            skArc(sketch, "E263", {"start": v(50.51, 4.2) * mm, "mid": v(50.63, 5.29) * mm, "end": v(51.2, 6.22) * mm});
            skArc(sketch, "E264", {"start": v(51.2, 6.21) * mm, "mid": v(51.73, 6.59) * mm, "end": v(52.35, 6.77) * mm});
            skArc(sketch, "E265", {"start": v(52.35, 6.77) * mm, "mid": v(54.2, 6.96) * mm, "end": v(56.05, 7.1) * mm});
            skArc(sketch, "E266", {"start": v(56.05, 7.1) * mm, "mid": v(58.64, 7.24) * mm, "end": v(61.23, 7.32) * mm});
            skArc(sketch, "E267", {"start": v(61.23, 7.32) * mm, "mid": v(64.9, 7.38) * mm, "end": v(68.58, 7.4) * mm});
            skArc(sketch, "E268", {"start": v(68.58, 7.4) * mm, "mid": v(74.4, 7.35) * mm, "end": v(80.22, 7.23) * mm});
            skArc(sketch, "E269", {"start": v(80.22, 7.23) * mm, "mid": v(83.05, 7) * mm, "end": v(85.84, 6.5) * mm});
            skArc(sketch, "E270", {"start": v(85.84, 6.5) * mm, "mid": v(88.83, 5.69) * mm, "end": v(91.74, 4.65) * mm});
            skArc(sketch, "E271", {"start": v(91.74, 4.65) * mm, "mid": v(99.27, 1.6) * mm, "end": v(106.8, -1.5) * mm});
            skArc(sketch, "E272", {"start": v(106.8, -1.5) * mm, "mid": v(108.93, -2.4) * mm, "end": v(111.06, -3.28) * mm});
            skArc(sketch, "E273", {"start": v(111.06, -3.28) * mm, "mid": v(112.93, -4.05) * mm, "end": v(114.8, -4.82) * mm});
            skArc(sketch, "E274", {"start": v(114.8, -4.82) * mm, "mid": v(116.4, -5.48) * mm, "end": v(118, -6.13) * mm});
            skArc(sketch, "E275", {"start": v(118, -6.13) * mm, "mid": v(118.29, -6.25) * mm, "end": v(118.58, -6.35) * mm});
            skArc(sketch, "E276", {"start": v(118.58, -6.35) * mm, "mid": v(118.74, -6.5) * mm, "end": v(118.74, -6.73) * mm});
            skArc(sketch, "E277", {"start": v(118.74, -6.73) * mm, "mid": v(118.08, -8.1) * mm, "end": v(117.41, -9.48) * mm});
            skArc(sketch, "E278", {"start": v(117.41, -9.48) * mm, "mid": v(116.57, -11.13) * mm, "end": v(115.69, -12.76) * mm});
            skArc(sketch, "E279", {"start": v(115.69, -12.76) * mm, "mid": v(114.6, -14.7) * mm, "end": v(113.49, -16.61) * mm});
            skArc(sketch, "E280", {"start": v(113.49, -16.61) * mm, "mid": v(112.03, -19.1) * mm, "end": v(110.59, -21.61) * mm});
            skArc(sketch, "E281", {"start": v(110.59, -21.61) * mm, "mid": v(108.58, -25.13) * mm, "end": v(106.58, -28.66) * mm});
            skArc(sketch, "E282", {"start": v(106.58, -28.66) * mm, "mid": v(104.42, -32.5) * mm, "end": v(102.26, -36.36) * mm});
            skArc(sketch, "E283", {"start": v(102.26, -36.36) * mm, "mid": v(100.24, -39.98) * mm, "end": v(98.24, -43.6) * mm});
            skArc(sketch, "E284", {"start": v(98.24, -43.6) * mm, "mid": v(96.16, -47.36) * mm, "end": v(94.08, -51.13) * mm});
            skArc(sketch, "E285", {"start": v(94.08, -51.13) * mm, "mid": v(91.7, -55.42) * mm, "end": v(89.33, -59.72) * mm});
            skArc(sketch, "E286", {"start": v(89.33, -59.72) * mm, "mid": v(87.03, -63.87) * mm, "end": v(84.73, -68.02) * mm});
            skArc(sketch, "E287", {"start": v(84.73, -68.02) * mm, "mid": v(82.9, -71.31) * mm, "end": v(81.08, -74.6) * mm});
            skArc(sketch, "E288", {"start": v(81.08, -74.6) * mm, "mid": v(77.18, -81.83) * mm, "end": v(73.45, -89.14) * mm});
            skArc(sketch, "E289", {"start": v(73.45, -89.14) * mm, "mid": v(70.46, -95.48) * mm, "end": v(67.73, -101.92) * mm});
            skArc(sketch, "E290", {"start": v(67.73, -101.92) * mm, "mid": v(65.34, -108.25) * mm, "end": v(63.2, -114.68) * mm});
            skArc(sketch, "E291", {"start": v(63.2, -114.68) * mm, "mid": v(61.1, -121.86) * mm, "end": v(59.2, -129.1) * mm});
            skArc(sketch, "E292", {"start": v(59.2, -129.1) * mm, "mid": v(58.72, -131.55) * mm, "end": v(58.46, -134.03) * mm});
            skArc(sketch, "E293", {"start": v(58.46, -134.03) * mm, "mid": v(58.35, -137.28) * mm, "end": v(58.38, -140.54) * mm});
            skArc(sketch, "E294", {"start": v(58.38, -140.54) * mm, "mid": v(58.54, -143.81) * mm, "end": v(58.85, -147.08) * mm});
            skArc(sketch, "E295", {"start": v(58.85, -147.08) * mm, "mid": v(59.26, -149.65) * mm, "end": v(59.88, -152.17) * mm});
            skArc(sketch, "E296", {"start": v(59.88, -152.17) * mm, "mid": v(61.41, -156.43) * mm, "end": v(63.45, -160.48) * mm});
            skArc(sketch, "E297", {"start": v(63.45, -160.48) * mm, "mid": v(66.06, -164.47) * mm, "end": v(69.06, -168.16) * mm});
            skArc(sketch, "E298", {"start": v(69.06, -168.16) * mm, "mid": v(72.6, -171.69) * mm, "end": v(76.47, -174.86) * mm});
            skArc(sketch, "E299", {"start": v(76.47, -174.86) * mm, "mid": v(80.8, -177.77) * mm, "end": v(85.36, -180.29) * mm});
            skArc(sketch, "E300", {"start": v(85.36, -180.29) * mm, "mid": v(89.87, -182.36) * mm, "end": v(94.49, -184.15) * mm});
            skArc(sketch, "E301", {"start": v(94.49, -184.15) * mm, "mid": v(98.19, -185.21) * mm, "end": v(102, -185.8) * mm});
            skArc(sketch, "E302", {"start": v(102, -185.8) * mm, "mid": v(105.4, -185.85) * mm, "end": v(108.76, -185.39) * mm});
            skArc(sketch, "E303", {"start": v(108.76, -185.39) * mm, "mid": v(112.23, -184.42) * mm, "end": v(115.54, -183.01) * mm});
            skArc(sketch, "E304", {"start": v(115.54, -183.01) * mm, "mid": v(117.5, -181.93) * mm, "end": v(119.35, -180.7) * mm});
            skArc(sketch, "E305", {"start": v(119.35, -180.7) * mm, "mid": v(121.38, -179.14) * mm, "end": v(123.32, -177.46) * mm});
            skArc(sketch, "E306", {"start": v(123.32, -177.46) * mm, "mid": v(125.09, -175.76) * mm, "end": v(126.76, -173.96) * mm});
            skArc(sketch, "E307", {"start": v(126.76, -173.96) * mm, "mid": v(127.92, -172.47) * mm, "end": v(128.9, -170.85) * mm});
            skArc(sketch, "E308", {"start": v(128.9, -170.85) * mm, "mid": v(129.26, -170.25) * mm, "end": v(129.68, -169.7) * mm});
            skArc(sketch, "E309", {"start": v(129.68, -169.7) * mm, "mid": v(130.25, -169.09) * mm, "end": v(130.86, -168.51) * mm});
            skArc(sketch, "E310", {"start": v(130.86, -168.51) * mm, "mid": v(131.53, -167.97) * mm, "end": v(132.22, -167.46) * mm});
            skArc(sketch, "E311", {"start": v(132.22, -167.46) * mm, "mid": v(132.88, -167.07) * mm, "end": v(133.57, -166.74) * mm});
            skArc(sketch, "E312", {"start": v(133.57, -166.74) * mm, "mid": v(135.12, -165.97) * mm, "end": v(136.56, -165) * mm});
            skArc(sketch, "E313", {"start": v(136.56, -165) * mm, "mid": v(137.77, -163.93) * mm, "end": v(138.8, -162.68) * mm});
            skArc(sketch, "E314", {"start": v(138.8, -162.68) * mm, "mid": v(140.01, -160.8) * mm, "end": v(141.06, -158.8) * mm});
            skArc(sketch, "E315", {"start": v(141.06, -158.8) * mm, "mid": v(142.85, -154.97) * mm, "end": v(144.58, -151.1) * mm});
            skArc(sketch, "E316", {"start": v(144.58, -151.1) * mm, "mid": v(147.12, -145.08) * mm, "end": v(149.48, -139) * mm});
            skArc(sketch, "E317", {"start": v(149.48, -139) * mm, "mid": v(152.14, -131.65) * mm, "end": v(154.67, -124.27) * mm});
            skArc(sketch, "E318", {"start": v(154.67, -124.27) * mm, "mid": v(157.4, -115.85) * mm, "end": v(160.01, -107.38) * mm});
            skArc(sketch, "E319", {"start": v(160.01, -107.38) * mm, "mid": v(162.76, -98.04) * mm, "end": v(165.4, -88.67) * mm});
            skArc(sketch, "E320", {"start": v(165.4, -88.67) * mm, "mid": v(168.83, -76.28) * mm, "end": v(172.3, -63.9) * mm});
            skArc(sketch, "E321", {"start": v(172.3, -63.9) * mm, "mid": v(174.36, -56.82) * mm, "end": v(176.54, -49.78) * mm});
            skArc(sketch, "E322", {"start": v(176.54, -49.78) * mm, "mid": v(178.32, -44.4) * mm, "end": v(180.24, -39.07) * mm});
            skArc(sketch, "E323", {"start": v(180.24, -39.07) * mm, "mid": v(182.44, -33.37) * mm, "end": v(184.76, -27.72) * mm});
            skArc(sketch, "E324", {"start": v(184.76, -27.72) * mm, "mid": v(187.36, -21.46) * mm, "end": v(189.87, -15.16) * mm});
            skArc(sketch, "E325", {"start": v(189.87, -15.16) * mm, "mid": v(191.38, -11.04) * mm, "end": v(192.7, -6.85) * mm});
            skArc(sketch, "E326", {"start": v(192.7, -6.85) * mm, "mid": v(193.53, -3.63) * mm, "end": v(194.14, -0.35) * mm});
            skArc(sketch, "E327", {"start": v(194.14, -0.35) * mm, "mid": v(194.49, 2.77) * mm, "end": v(194.58, 5.9) * mm});
            skArc(sketch, "E328", {"start": v(194.58, 5.9) * mm, "mid": v(193.95, 12.1) * mm, "end": v(192.18, 18.07) * mm});
            skArc(sketch, "E329", {"start": v(192.18, 18.07) * mm, "mid": v(189.3, 23.8) * mm, "end": v(185.49, 28.95) * mm});
            skArc(sketch, "E330", {"start": v(185.49, 28.95) * mm, "mid": v(180.89, 33.34) * mm, "end": v(175.6, 36.89) * mm});
            skArc(sketch, "E331", {"start": v(175.6, 36.89) * mm, "mid": v(169.99, 39.32) * mm, "end": v(164.01, 40.62) * mm});
            skArc(sketch, "E332", {"start": v(164.01, 40.62) * mm, "mid": v(162.95, 40.77) * mm, "end": v(161.9, 40.99) * mm});
            skArc(sketch, "E333", {"start": v(161.9, 40.99) * mm, "mid": v(160.88, 41.25) * mm, "end": v(159.89, 41.57) * mm});
            skArc(sketch, "E334", {"start": v(159.89, 41.57) * mm, "mid": v(159.03, 41.9) * mm, "end": v(158.2, 42.29) * mm});
            skArc(sketch, "E335", {"start": v(158.2, 42.29) * mm, "mid": v(157.64, 42.63) * mm, "end": v(157.13, 43.06) * mm});
            skArc(sketch, "E336", {"start": v(157.13, 43.06) * mm, "mid": v(156.24, 43.8) * mm, "end": v(155.22, 44.36) * mm});
            skArc(sketch, "E337", {"start": v(155.22, 44.36) * mm, "mid": v(154.12, 44.7) * mm, "end": v(152.98, 44.83) * mm});
            skArc(sketch, "E338", {"start": v(152.98, 44.83) * mm, "mid": v(151.87, 44.73) * mm, "end": v(150.8, 44.4) * mm});
            skArc(sketch, "E339", {"start": v(150.8, 44.4) * mm, "mid": v(149.86, 43.88) * mm, "end": v(149.06, 43.15) * mm});
            skArc(sketch, "E340", {"start": v(149.06, 43.15) * mm, "mid": v(148.64, 42.64) * mm, "end": v(148.27, 42.09) * mm});
            skArc(sketch, "E341", {"start": v(148.27, 42.09) * mm, "mid": v(147.64, 41.05) * mm, "end": v(147.02, 40) * mm});
            skArc(sketch, "E342", {"start": v(147.02, 40) * mm, "mid": v(146.32, 38.77) * mm, "end": v(145.64, 37.52) * mm});
            skArc(sketch, "E343", {"start": v(145.64, 37.52) * mm, "mid": v(144.95, 36.21) * mm, "end": v(144.29, 34.9) * mm});
            skArc(sketch, "E344", {"start": v(144.29, 34.9) * mm, "mid": v(143.47, 33.28) * mm, "end": v(142.61, 31.67) * mm});
            skArc(sketch, "E345", {"start": v(142.61, 31.67) * mm, "mid": v(141.38, 29.42) * mm, "end": v(140.12, 27.17) * mm});
            skArc(sketch, "E346", {"start": v(140.12, 27.17) * mm, "mid": v(138.74, 24.72) * mm, "end": v(137.34, 22.28) * mm});
            skArc(sketch, "E347", {"start": v(137.34, 22.28) * mm, "mid": v(136, 19.99) * mm, "end": v(134.65, 17.7) * mm});
            skLineSegment(sketch, "E348", {"start": v(134.65, 17.7) * mm, "end": v(128.23, 7.01) * mm});
            skLineSegment(sketch, "E349", {"start": v(128.23, 7.01) * mm, "end": v(121.82, 11.49) * mm});
            skArc(sketch, "E350", {"start": v(121.82, 11.49) * mm, "mid": v(118.3, 13.82) * mm, "end": v(114.64, 15.96) * mm});
            skArc(sketch, "E351", {"start": v(114.64, 15.96) * mm, "mid": v(110.22, 18.3) * mm, "end": v(105.73, 20.5) * mm});
            skArc(sketch, "E352", {"start": v(105.73, 20.5) * mm, "mid": v(101.18, 22.54) * mm, "end": v(96.56, 24.44) * mm});
            skArc(sketch, "E353", {"start": v(96.56, 24.44) * mm, "mid": v(92.64, 25.85) * mm, "end": v(88.65, 27.05) * mm});
            skArc(sketch, "E354", {"start": v(88.65, 27.05) * mm, "mid": v(84.75, 27.93) * mm, "end": v(80.8, 28.49) * mm});
            skArc(sketch, "E355", {"start": v(80.8, 28.49) * mm, "mid": v(75.16, 28.97) * mm, "end": v(69.5, 29.28) * mm});
            skArc(sketch, "E356", {"start": v(69.5, 29.28) * mm, "mid": v(63.88, 29.42) * mm, "end": v(58.25, 29.4) * mm});
            skArc(sketch, "E357", {"start": v(58.25, 29.4) * mm, "mid": v(54.4, 29.15) * mm, "end": v(50.58, 28.57) * mm});
            skArc(sketch, "E358", {"start": v(50.58, 28.57) * mm, "mid": v(49.3, 28.33) * mm, "end": v(48.03, 28.13) * mm});
            skArc(sketch, "E359", {"start": v(48.03, 28.13) * mm, "mid": v(47.48, 28.11) * mm, "end": v(46.93, 28.22) * mm});
            skArc(sketch, "E360", {"start": v(46.93, 28.22) * mm, "mid": v(46.56, 28.43) * mm, "end": v(46.3, 28.77) * mm});
            skArc(sketch, "E361", {"start": v(46.3, 28.77) * mm, "mid": v(46.06, 29.4) * mm, "end": v(45.88, 30.07) * mm});
            skArc(sketch, "E362", {"start": v(45.88, 30.07) * mm, "mid": v(45.72, 30.87) * mm, "end": v(45.56, 31.68) * mm});
            skArc(sketch, "E363", {"start": v(45.56, 31.68) * mm, "mid": v(45.03, 34.42) * mm, "end": v(44.5, 37.15) * mm});
            skArc(sketch, "E364", {"start": v(44.5, 37.15) * mm, "mid": v(43.86, 40.4) * mm, "end": v(43.24, 43.64) * mm});
            skArc(sketch, "E365", {"start": v(43.24, 43.64) * mm, "mid": v(42.54, 47.27) * mm, "end": v(41.84, 50.9) * mm});
            skArc(sketch, "E366", {"start": v(41.84, 50.9) * mm, "mid": v(41.14, 54.52) * mm, "end": v(40.43, 58.13) * mm});
            skArc(sketch, "E367", {"start": v(40.43, 58.13) * mm, "mid": v(39.8, 61.35) * mm, "end": v(39.16, 64.56) * mm});
            skArc(sketch, "E368", {"start": v(39.16, 64.56) * mm, "mid": v(38.62, 67.27) * mm, "end": v(38.07, 69.98) * mm});
            skArc(sketch, "E369", {"start": v(38.07, 69.98) * mm, "mid": v(37.91, 70.7) * mm, "end": v(37.73, 71.42) * mm});
            skArc(sketch, "E370", {"start": v(37.73, 71.42) * mm, "mid": v(37.63, 71.95) * mm, "end": v(37.6, 72.5) * mm});
            skArc(sketch, "E371", {"start": v(37.6, 72.5) * mm, "mid": v(37.71, 72.85) * mm, "end": v(37.97, 73.1) * mm});
            skArc(sketch, "E372", {"start": v(37.97, 73.1) * mm, "mid": v(38.44, 73.32) * mm, "end": v(38.94, 73.42) * mm});
            skArc(sketch, "E373", {"start": v(38.94, 73.42) * mm, "mid": v(40.1, 73.5) * mm, "end": v(41.26, 73.54) * mm});
            skArc(sketch, "E374", {"start": v(41.26, 73.54) * mm, "mid": v(45.23, 74) * mm, "end": v(49.07, 75.14) * mm});
            skArc(sketch, "E375", {"start": v(49.07, 75.14) * mm, "mid": v(52.74, 76.95) * mm, "end": v(56.07, 79.34) * mm});
            skArc(sketch, "E376", {"start": v(56.07, 79.34) * mm, "mid": v(59.12, 82.38) * mm, "end": v(61.67, 85.85) * mm});
            skArc(sketch, "E377", {"start": v(61.67, 85.85) * mm, "mid": v(63.82, 89.85) * mm, "end": v(65.42, 94.1) * mm});
            skArc(sketch, "E378", {"start": v(65.42, 94.1) * mm, "mid": v(66.96, 101.84) * mm, "end": v(66.95, 109.71) * mm});
            skArc(sketch, "E379", {"start": v(66.95, 109.71) * mm, "mid": v(65.37, 117.13) * mm, "end": v(62.2, 124.02) * mm});
            skArc(sketch, "E380", {"start": v(62.2, 124.02) * mm, "mid": v(57.39, 130.46) * mm, "end": v(51.37, 135.78) * mm});
            skArc(sketch, "E381", {"start": v(51.37, 135.78) * mm, "mid": v(43.7, 140.49) * mm, "end": v(35.43, 144.02) * mm});
            skArc(sketch, "E382", {"start": v(35.43, 144.02) * mm, "mid": v(34.3, 144.4) * mm, "end": v(33.17, 144.74) * mm});
            skArc(sketch, "E383", {"start": v(33.17, 144.74) * mm, "mid": v(32.04, 145.06) * mm, "end": v(30.9, 145.35) * mm});
            skArc(sketch, "E384", {"start": v(30.9, 145.35) * mm, "mid": v(29.9, 145.58) * mm, "end": v(28.89, 145.78) * mm});
            skArc(sketch, "E385", {"start": v(28.89, 145.78) * mm, "mid": v(28.26, 145.87) * mm, "end": v(27.64, 145.9) * mm});
            skLineSegment(sketch, "E386", {"start": v(27.64, 145.9) * mm, "end": v(25.3, 145.9) * mm});
            skLineSegment(sketch, "E387", {"start": v(25.3, 145.9) * mm, "end": v(25.54, 163.78) * mm});
            skArc(sketch, "E388", {"start": v(25.54, 163.78) * mm, "mid": v(25.6, 169.14) * mm, "end": v(25.64, 174.49) * mm});
            skArc(sketch, "E389", {"start": v(25.64, 174.49) * mm, "mid": v(25.6, 176.85) * mm, "end": v(25.45, 179.2) * mm});
            skArc(sketch, "E390", {"start": v(25.45, 179.2) * mm, "mid": v(25.27, 180.57) * mm, "end": v(24.94, 181.92) * mm});
            skArc(sketch, "E391", {"start": v(24.94, 181.92) * mm, "mid": v(24.51, 182.9) * mm, "end": v(23.89, 183.78) * mm});
            skArc(sketch, "E392", {"start": v(23.89, 183.78) * mm, "mid": v(22.93, 184.62) * mm, "end": v(21.81, 185.22) * mm});
            skArc(sketch, "E393", {"start": v(21.81, 185.22) * mm, "mid": v(20.4, 185.65) * mm, "end": v(18.96, 185.87) * mm});
            skArc(sketch, "E394", {"start": v(18.96, 185.87) * mm, "mid": v(17.56, 185.86) * mm, "end": v(16.18, 185.62) * mm});
            skArc(sketch, "E395", {"start": v(16.18, 185.62) * mm, "mid": v(15.17, 185.19) * mm, "end": v(14.34, 184.46) * mm});
            skArc(sketch, "E396", {"start": v(-63.8, 28.98) * mm, "mid": v(-61.4, 26.29) * mm, "end": v(-59.51, 23.2) * mm});
            skArc(sketch, "E397", {"start": v(-59.51, 23.2) * mm, "mid": v(-57.65, 18.95) * mm, "end": v(-56.18, 14.56) * mm});
            skArc(sketch, "E398", {"start": v(-56.18, 14.56) * mm, "mid": v(-55.06, 9.94) * mm, "end": v(-54.35, 5.24) * mm});
            skArc(sketch, "E399", {"start": v(-54.35, 5.24) * mm, "mid": v(-54.2, 1.25) * mm, "end": v(-54.66, -2.72) * mm});
            skArc(sketch, "E400", {"start": v(-54.66, -2.72) * mm, "mid": v(-54.93, -3.8) * mm, "end": v(-55.34, -4.85) * mm});
            skArc(sketch, "E401", {"start": v(-55.34, -4.85) * mm, "mid": v(-56.19, -6.63) * mm, "end": v(-57.09, -8.4) * mm});
            skArc(sketch, "E402", {"start": v(-57.09, -8.4) * mm, "mid": v(-58.2, -10.45) * mm, "end": v(-59.38, -12.48) * mm});
            skArc(sketch, "E403", {"start": v(-59.38, -12.48) * mm, "mid": v(-60.67, -14.6) * mm, "end": v(-62, -16.67) * mm});
            skArc(sketch, "E404", {"start": v(-62, -16.67) * mm, "mid": v(-65.46, -22.08) * mm, "end": v(-68.78, -27.58) * mm});
            skArc(sketch, "E405", {"start": v(-68.78, -27.58) * mm, "mid": v(-72.4, -33.86) * mm, "end": v(-75.9, -40.2) * mm});
            skArc(sketch, "E406", {"start": v(-75.9, -40.2) * mm, "mid": v(-79.57, -47.13) * mm, "end": v(-83.13, -54.11) * mm});
            skArc(sketch, "E407", {"start": v(-83.13, -54.11) * mm, "mid": v(-86.74, -61.49) * mm, "end": v(-90.25, -68.92) * mm});
            skArc(sketch, "E408", {"start": v(-90.25, -68.92) * mm, "mid": v(-91.95, -72.57) * mm, "end": v(-93.64, -76.21) * mm});
            skArc(sketch, "E409", {"start": v(-93.64, -76.21) * mm, "mid": v(-95.54, -80.28) * mm, "end": v(-97.44, -84.35) * mm});
            skArc(sketch, "E410", {"start": v(-97.44, -84.35) * mm, "mid": v(-99.25, -88.22) * mm, "end": v(-101.06, -92.09) * mm});
            skArc(sketch, "E411", {"start": v(-101.06, -92.09) * mm, "mid": v(-102.46, -95.06) * mm, "end": v(-103.86, -98.03) * mm});
            skLineSegment(sketch, "E412", {"start": v(-103.86, -98.03) * mm, "end": v(-109.73, -110.45) * mm});
            skLineSegment(sketch, "E413", {"start": v(-109.73, -110.45) * mm, "end": v(-112.54, -106.03) * mm});
            skArc(sketch, "E414", {"start": v(-112.54, -106.03) * mm, "mid": v(-114.28, -103.54) * mm, "end": v(-116.23, -101.22) * mm});
            skArc(sketch, "E415", {"start": v(-116.23, -101.22) * mm, "mid": v(-118.6, -98.8) * mm, "end": v(-121.12, -96.53) * mm});
            skArc(sketch, "E416", {"start": v(-121.12, -96.53) * mm, "mid": v(-123.72, -94.47) * mm, "end": v(-126.46, -92.58) * mm});
            skArc(sketch, "E417", {"start": v(-126.46, -92.58) * mm, "mid": v(-128.92, -91.17) * mm, "end": v(-131.5, -90.03) * mm});
            skArc(sketch, "E418", {"start": v(-131.5, -90.03) * mm, "mid": v(-132.84, -89.56) * mm, "end": v(-134.2, -89.16) * mm});
            skArc(sketch, "E419", {"start": v(-134.2, -89.16) * mm, "mid": v(-135.92, -88.73) * mm, "end": v(-137.64, -88.34) * mm});
            skArc(sketch, "E420", {"start": v(-137.64, -88.34) * mm, "mid": v(-139.42, -88) * mm, "end": v(-141.21, -87.7) * mm});
            skArc(sketch, "E421", {"start": v(-141.21, -87.7) * mm, "mid": v(-142.79, -87.5) * mm, "end": v(-144.37, -87.35) * mm});
            skLineSegment(sketch, "E422", {"start": v(-144.37, -87.35) * mm, "end": v(-151.54, -86.85) * mm});
            skLineSegment(sketch, "E423", {"start": v(-151.54, -86.85) * mm, "end": v(-145.23, -77.72) * mm});
            skArc(sketch, "E424", {"start": v(-145.23, -77.72) * mm, "mid": v(-140.72, -71.05) * mm, "end": v(-136.35, -64.29) * mm});
            skArc(sketch, "E425", {"start": v(-136.35, -64.29) * mm, "mid": v(-128.02, -51.09) * mm, "end": v(-119.74, -37.86) * mm});
            skArc(sketch, "E426", {"start": v(-119.74, -37.86) * mm, "mid": v(-111.33, -24.32) * mm, "end": v(-102.98, -10.75) * mm});
            skArc(sketch, "E427", {"start": v(-102.98, -10.75) * mm, "mid": v(-97.23, -1.26) * mm, "end": v(-91.58, 8.3) * mm});
            skArc(sketch, "E428", {"start": v(-91.58, 8.3) * mm, "mid": v(-89.56, 11.7) * mm, "end": v(-87.5, 15.09) * mm});
            skArc(sketch, "E429", {"start": v(-87.5, 15.09) * mm, "mid": v(-85.53, 18.22) * mm, "end": v(-83.52, 21.33) * mm});
            skArc(sketch, "E430", {"start": v(-83.52, 21.33) * mm, "mid": v(-81.8, 23.92) * mm, "end": v(-80.03, 26.48) * mm});
            skArc(sketch, "E431", {"start": v(-80.03, 26.48) * mm, "mid": v(-79.15, 27.61) * mm, "end": v(-78.17, 28.65) * mm});
            skArc(sketch, "E432", {"start": v(-78.17, 28.65) * mm, "mid": v(-76.48, 30.02) * mm, "end": v(-74.62, 31.12) * mm});
            skArc(sketch, "E433", {"start": v(-74.62, 31.12) * mm, "mid": v(-72.82, 31.78) * mm, "end": v(-70.92, 32.03) * mm});
            skArc(sketch, "E434", {"start": v(-70.92, 32.03) * mm, "mid": v(-69.05, 31.86) * mm, "end": v(-67.26, 31.29) * mm});
            skArc(sketch, "E435", {"start": v(-67.26, 31.29) * mm, "mid": v(-65.43, 30.28) * mm, "end": v(-63.8, 28.98) * mm});
            skArc(sketch, "E436", {"start": v(165.5, 24.38) * mm, "mid": v(167.56, 22.81) * mm, "end": v(169.38, 20.98) * mm});
            skArc(sketch, "E437", {"start": v(169.38, 20.98) * mm, "mid": v(170.82, 19.03) * mm, "end": v(171.92, 16.87) * mm});
            skArc(sketch, "E438", {"start": v(171.92, 16.87) * mm, "mid": v(172.8, 14.25) * mm, "end": v(173.32, 11.54) * mm});
            skArc(sketch, "E439", {"start": v(173.32, 11.54) * mm, "mid": v(173.65, 7.98) * mm, "end": v(173.76, 4.4) * mm});
            skArc(sketch, "E440", {"start": v(173.76, 4.4) * mm, "mid": v(173.65, 0.67) * mm, "end": v(173.36, -3.05) * mm});
            skArc(sketch, "E441", {"start": v(173.36, -3.05) * mm, "mid": v(172.89, -6.44) * mm, "end": v(172.19, -9.8) * mm});
            skArc(sketch, "E442", {"start": v(172.19, -9.8) * mm, "mid": v(171.06, -14.02) * mm, "end": v(169.75, -18.2) * mm});
            skArc(sketch, "E443", {"start": v(169.75, -18.2) * mm, "mid": v(167.34, -25.22) * mm, "end": v(164.86, -32.22) * mm});
            skArc(sketch, "E444", {"start": v(164.86, -32.22) * mm, "mid": v(163.46, -36.2) * mm, "end": v(162.13, -40.2) * mm});
            skArc(sketch, "E445", {"start": v(162.13, -40.2) * mm, "mid": v(160.2, -46.19) * mm, "end": v(158.31, -52.19) * mm});
            skArc(sketch, "E446", {"start": v(158.31, -52.19) * mm, "mid": v(156.23, -58.9) * mm, "end": v(154.19, -65.6) * mm});
            skArc(sketch, "E447", {"start": v(154.19, -65.6) * mm, "mid": v(152.25, -72.1) * mm, "end": v(150.34, -78.6) * mm});
            skArc(sketch, "E448", {"start": v(150.34, -78.6) * mm, "mid": v(146.5, -91.72) * mm, "end": v(142.62, -104.82) * mm});
            skArc(sketch, "E449", {"start": v(142.62, -104.82) * mm, "mid": v(140.17, -112.76) * mm, "end": v(137.57, -120.65) * mm});
            skArc(sketch, "E450", {"start": v(137.57, -120.65) * mm, "mid": v(135.83, -125.64) * mm, "end": v(134, -130.6) * mm});
            skArc(sketch, "E451", {"start": v(134, -130.6) * mm, "mid": v(133.37, -131.03) * mm, "end": v(132.74, -130.6) * mm});
            skArc(sketch, "E452", {"start": v(132.74, -130.6) * mm, "mid": v(130.9, -126.2) * mm, "end": v(128.85, -121.9) * mm});
            skArc(sketch, "E453", {"start": v(128.85, -121.9) * mm, "mid": v(126.81, -118.19) * mm, "end": v(124.51, -114.64) * mm});
            skArc(sketch, "E454", {"start": v(124.51, -114.64) * mm, "mid": v(122.14, -111.5) * mm, "end": v(119.53, -108.56) * mm});
            skArc(sketch, "E455", {"start": v(119.53, -108.56) * mm, "mid": v(116.73, -105.85) * mm, "end": v(113.73, -103.37) * mm});
            skArc(sketch, "E456", {"start": v(113.73, -103.37) * mm, "mid": v(111.62, -101.88) * mm, "end": v(109.4, -100.55) * mm});
            skArc(sketch, "E457", {"start": v(109.4, -100.55) * mm, "mid": v(106.97, -99.3) * mm, "end": v(104.46, -98.2) * mm});
            skArc(sketch, "E458", {"start": v(104.46, -98.2) * mm, "mid": v(102.06, -97.33) * mm, "end": v(99.61, -96.61) * mm});
            skArc(sketch, "E459", {"start": v(99.61, -96.61) * mm, "mid": v(97.63, -96.23) * mm, "end": v(95.6, -96.1) * mm});
            skArc(sketch, "E460", {"start": v(95.6, -96.1) * mm, "mid": v(95.16, -96.09) * mm, "end": v(94.72, -96.05) * mm});
            skArc(sketch, "E461", {"start": v(94.72, -96.05) * mm, "mid": v(94.34, -95.99) * mm, "end": v(93.97, -95.9) * mm});
            skArc(sketch, "E462", {"start": v(93.97, -95.9) * mm, "mid": v(93.7, -95.8) * mm, "end": v(93.45, -95.67) * mm});
            skArc(sketch, "E463", {"start": v(93.45, -95.67) * mm, "mid": v(93.33, -95.56) * mm, "end": v(93.3, -95.4) * mm});
            skArc(sketch, "E464", {"start": v(93.3, -95.4) * mm, "mid": v(93.32, -95.15) * mm, "end": v(93.4, -94.91) * mm});
            skArc(sketch, "E465", {"start": v(93.4, -94.91) * mm, "mid": v(93.99, -93.65) * mm, "end": v(94.58, -92.4) * mm});
            skArc(sketch, "E466", {"start": v(94.58, -92.4) * mm, "mid": v(95.28, -90.94) * mm, "end": v(96, -89.48) * mm});
            skArc(sketch, "E467", {"start": v(96, -89.48) * mm, "mid": v(96.84, -87.82) * mm, "end": v(97.68, -86.15) * mm});
            skArc(sketch, "E468", {"start": v(97.68, -86.15) * mm, "mid": v(98.7, -84.13) * mm, "end": v(99.7, -82.1) * mm});
            skArc(sketch, "E469", {"start": v(99.7, -82.1) * mm, "mid": v(100.95, -79.5) * mm, "end": v(102.18, -76.88) * mm});
            skArc(sketch, "E470", {"start": v(102.18, -76.88) * mm, "mid": v(103.44, -74.16) * mm, "end": v(104.68, -71.44) * mm});
            skArc(sketch, "E471", {"start": v(104.68, -71.44) * mm, "mid": v(105.76, -69.02) * mm, "end": v(106.82, -66.6) * mm});
            skArc(sketch, "E472", {"start": v(106.82, -66.6) * mm, "mid": v(109.57, -60.36) * mm, "end": v(112.43, -54.16) * mm});
            skArc(sketch, "E473", {"start": v(112.43, -54.16) * mm, "mid": v(115.31, -48.18) * mm, "end": v(118.3, -42.25) * mm});
            skArc(sketch, "E474", {"start": v(118.3, -42.25) * mm, "mid": v(121.51, -36.13) * mm, "end": v(124.83, -30.07) * mm});
            skArc(sketch, "E475", {"start": v(124.83, -30.07) * mm, "mid": v(128.6, -23.42) * mm, "end": v(132.44, -16.83) * mm});
            skArc(sketch, "E476", {"start": v(132.44, -16.83) * mm, "mid": v(135.98, -10.76) * mm, "end": v(139.44, -4.64) * mm});
            skArc(sketch, "E477", {"start": v(139.44, -4.64) * mm, "mid": v(142.76, 1.43) * mm, "end": v(146, 7.56) * mm});
            skArc(sketch, "E478", {"start": v(146, 7.56) * mm, "mid": v(148.73, 12.9) * mm, "end": v(151.39, 18.26) * mm});
            skArc(sketch, "E479", {"start": v(151.39, 18.26) * mm, "mid": v(152.85, 21.52) * mm, "end": v(154.12, 24.85) * mm});
            skArc(sketch, "E480", {"start": v(154.12, 24.85) * mm, "mid": v(154.49, 25.82) * mm, "end": v(154.9, 26.76) * mm});
            skArc(sketch, "E481", {"start": v(154.9, 26.76) * mm, "mid": v(155.19, 27.2) * mm, "end": v(155.6, 27.55) * mm});
            skArc(sketch, "E482", {"start": v(155.6, 27.55) * mm, "mid": v(156.08, 27.74) * mm, "end": v(156.6, 27.78) * mm});
            skArc(sketch, "E483", {"start": v(156.6, 27.78) * mm, "mid": v(157.56, 27.67) * mm, "end": v(158.52, 27.5) * mm});
            skArc(sketch, "E484", {"start": v(158.52, 27.5) * mm, "mid": v(159.28, 27.32) * mm, "end": v(160.03, 27.08) * mm});
            skArc(sketch, "E485", {"start": v(160.03, 27.08) * mm, "mid": v(160.97, 26.72) * mm, "end": v(161.9, 26.32) * mm});
            skArc(sketch, "E486", {"start": v(161.9, 26.32) * mm, "mid": v(162.88, 25.86) * mm, "end": v(163.83, 25.37) * mm});
            skArc(sketch, "E487", {"start": v(163.83, 25.37) * mm, "mid": v(164.68, 24.9) * mm, "end": v(165.5, 24.38) * mm});
            skArc(sketch, "E488", {"start": v(-140.07, -105.63) * mm, "mid": v(-136.72, -107.57) * mm, "end": v(-133.69, -109.97) * mm});
            skArc(sketch, "E489", {"start": v(-133.69, -109.97) * mm, "mid": v(-130.5, -113.17) * mm, "end": v(-127.62, -116.64) * mm});
            skArc(sketch, "E490", {"start": v(-127.62, -116.64) * mm, "mid": v(-125.2, -120.16) * mm, "end": v(-123.13, -123.9) * mm});
            skArc(sketch, "E491", {"start": v(-123.13, -123.9) * mm, "mid": v(-122.07, -126.82) * mm, "end": v(-121.7, -129.92) * mm});
            skArc(sketch, "E492", {"start": v(-121.7, -129.92) * mm, "mid": v(-121.97, -131.78) * mm, "end": v(-122.74, -133.5) * mm});
            skArc(sketch, "E493", {"start": v(-122.74, -133.5) * mm, "mid": v(-125.04, -137.04) * mm, "end": v(-127.46, -140.51) * mm});
            skArc(sketch, "E494", {"start": v(-127.46, -140.51) * mm, "mid": v(-130.19, -144.14) * mm, "end": v(-133.07, -147.65) * mm});
            skArc(sketch, "E495", {"start": v(-133.07, -147.65) * mm, "mid": v(-135.63, -150.44) * mm, "end": v(-138.39, -153.05) * mm});
            skArc(sketch, "E496", {"start": v(-138.39, -153.05) * mm, "mid": v(-141.27, -155.28) * mm, "end": v(-144.42, -157.13) * mm});
            skArc(sketch, "E497", {"start": v(-144.42, -157.13) * mm, "mid": v(-147.64, -158.46) * mm, "end": v(-151.01, -159.31) * mm});
            skArc(sketch, "E498", {"start": v(-151.01, -159.31) * mm, "mid": v(-154.33, -159.63) * mm, "end": v(-157.65, -159.43) * mm});
            skArc(sketch, "E499", {"start": v(-157.65, -159.43) * mm, "mid": v(-160.83, -158.72) * mm, "end": v(-163.84, -157.5) * mm});
            skArc(sketch, "E500", {"start": v(-163.84, -157.5) * mm, "mid": v(-165.6, -156.44) * mm, "end": v(-167.17, -155.14) * mm});
            skArc(sketch, "E501", {"start": v(-167.17, -155.14) * mm, "mid": v(-169.07, -153.18) * mm, "end": v(-170.84, -151.1) * mm});
            skArc(sketch, "E502", {"start": v(-170.84, -151.1) * mm, "mid": v(-172.49, -148.89) * mm, "end": v(-174, -146.58) * mm});
            skArc(sketch, "E503", {"start": v(-174, -146.58) * mm, "mid": v(-174.98, -144.68) * mm, "end": v(-175.7, -142.66) * mm});
            skArc(sketch, "E504", {"start": v(-175.7, -142.66) * mm, "mid": v(-176.35, -139.69) * mm, "end": v(-176.7, -136.66) * mm});
            skArc(sketch, "E505", {"start": v(-176.7, -136.66) * mm, "mid": v(-176.73, -133.4) * mm, "end": v(-176.49, -130.14) * mm});
            skArc(sketch, "E506", {"start": v(-176.49, -130.14) * mm, "mid": v(-175.95, -126.84) * mm, "end": v(-175.13, -123.6) * mm});
            skArc(sketch, "E507", {"start": v(-175.13, -123.6) * mm, "mid": v(-174.04, -120.51) * mm, "end": v(-172.68, -117.53) * mm});
            skArc(sketch, "E508", {"start": v(-172.68, -117.53) * mm, "mid": v(-169.87, -112.92) * mm, "end": v(-166.43, -108.77) * mm});
            skArc(sketch, "E509", {"start": v(-166.43, -108.77) * mm, "mid": v(-162.86, -105.81) * mm, "end": v(-158.72, -103.74) * mm});
            skArc(sketch, "E510", {"start": v(-158.72, -103.74) * mm, "mid": v(-154.33, -102.7) * mm, "end": v(-149.82, -102.73) * mm});
            skArc(sketch, "E511", {"start": v(-149.82, -102.73) * mm, "mid": v(-144.82, -103.78) * mm, "end": v(-140.07, -105.63) * mm});
            skArc(sketch, "E512", {"start": v(103.52, -113.7) * mm, "mid": v(105.42, -115.2) * mm, "end": v(107.16, -116.88) * mm});
            skArc(sketch, "E513", {"start": v(107.16, -116.88) * mm, "mid": v(108.98, -118.96) * mm, "end": v(110.67, -121.17) * mm});
            skArc(sketch, "E514", {"start": v(110.67, -121.17) * mm, "mid": v(112.33, -123.67) * mm, "end": v(113.83, -126.27) * mm});
            skArc(sketch, "E515", {"start": v(113.83, -126.27) * mm, "mid": v(115.21, -129.03) * mm, "end": v(116.43, -131.86) * mm});
            skArc(sketch, "E516", {"start": v(116.43, -131.86) * mm, "mid": v(117.04, -133.53) * mm, "end": v(117.56, -135.23) * mm});
            skArc(sketch, "E517", {"start": v(117.56, -135.23) * mm, "mid": v(117.96, -136.83) * mm, "end": v(118.25, -138.46) * mm});
            skArc(sketch, "E518", {"start": v(118.25, -138.46) * mm, "mid": v(118.48, -140.36) * mm, "end": v(118.62, -142.27) * mm});
            skArc(sketch, "E519", {"start": v(118.62, -142.27) * mm, "mid": v(118.7, -144.94) * mm, "end": v(118.75, -147.6) * mm});
            skArc(sketch, "E520", {"start": v(118.75, -147.6) * mm, "mid": v(118.74, -150.48) * mm, "end": v(118.7, -153.36) * mm});
            skArc(sketch, "E521", {"start": v(118.7, -153.36) * mm, "mid": v(118.6, -154.92) * mm, "end": v(118.4, -156.46) * mm});
            skArc(sketch, "E522", {"start": v(118.4, -156.46) * mm, "mid": v(118.14, -157.58) * mm, "end": v(117.74, -158.65) * mm});
            skArc(sketch, "E523", {"start": v(117.74, -158.65) * mm, "mid": v(117.17, -159.76) * mm, "end": v(116.5, -160.8) * mm});
            skArc(sketch, "E524", {"start": v(116.5, -160.8) * mm, "mid": v(115.07, -162.47) * mm, "end": v(113.37, -163.85) * mm});
            skArc(sketch, "E525", {"start": v(113.37, -163.85) * mm, "mid": v(110.64, -165.57) * mm, "end": v(107.81, -167.13) * mm});
            skArc(sketch, "E526", {"start": v(107.81, -167.13) * mm, "mid": v(104.9, -168.5) * mm, "end": v(101.93, -169.7) * mm});
            skArc(sketch, "E527", {"start": v(101.93, -169.7) * mm, "mid": v(99.87, -170.25) * mm, "end": v(97.75, -170.4) * mm});
            skArc(sketch, "E528", {"start": v(97.75, -170.4) * mm, "mid": v(94.51, -169.94) * mm, "end": v(91.46, -168.8) * mm});
            skArc(sketch, "E529", {"start": v(91.46, -168.8) * mm, "mid": v(87.9, -166.72) * mm, "end": v(84.6, -164.27) * mm});
            skArc(sketch, "E530", {"start": v(84.6, -164.27) * mm, "mid": v(81.3, -161.2) * mm, "end": v(78.32, -157.79) * mm});
            skArc(sketch, "E531", {"start": v(78.32, -157.79) * mm, "mid": v(75.8, -154.17) * mm, "end": v(73.68, -150.28) * mm});
            skArc(sketch, "E532", {"start": v(73.68, -150.28) * mm, "mid": v(72.23, -146.37) * mm, "end": v(71.46, -142.26) * mm});
            skArc(sketch, "E533", {"start": v(71.46, -142.26) * mm, "mid": v(71.34, -137.81) * mm, "end": v(71.84, -133.4) * mm});
            skArc(sketch, "E534", {"start": v(71.84, -133.4) * mm, "mid": v(73, -128.94) * mm, "end": v(74.76, -124.68) * mm});
            skArc(sketch, "E535", {"start": v(74.76, -124.68) * mm, "mid": v(77.08, -120.7) * mm, "end": v(79.93, -117.08) * mm});
            skArc(sketch, "E536", {"start": v(79.93, -117.08) * mm, "mid": v(80.76, -116.19) * mm, "end": v(81.63, -115.34) * mm});
            skArc(sketch, "E537", {"start": v(81.63, -115.34) * mm, "mid": v(82.57, -114.48) * mm, "end": v(83.54, -113.65) * mm});
            skArc(sketch, "E538", {"start": v(83.54, -113.65) * mm, "mid": v(84.44, -112.93) * mm, "end": v(85.37, -112.25) * mm});
            skArc(sketch, "E539", {"start": v(85.37, -112.25) * mm, "mid": v(86.06, -111.8) * mm, "end": v(86.8, -111.43) * mm});
            skArc(sketch, "E540", {"start": v(86.8, -111.43) * mm, "mid": v(88.66, -110.76) * mm, "end": v(90.6, -110.41) * mm});
            skArc(sketch, "E541", {"start": v(90.6, -110.41) * mm, "mid": v(92.85, -110.33) * mm, "end": v(95.1, -110.5) * mm});
            skArc(sketch, "E542", {"start": v(95.1, -110.5) * mm, "mid": v(97.38, -110.95) * mm, "end": v(99.6, -111.64) * mm});
            skArc(sketch, "E543", {"start": v(99.6, -111.64) * mm, "mid": v(101.63, -112.55) * mm, "end": v(103.52, -113.7) * mm});
            skSolve(sketch);
        }
        {
            var Q0;
            Q0=qSketchRegion(id+"F3",true);
            var Q1;
            Q1=sQuery(id+"F3.wireOp",EDGE,"c928f899-12af-4b01-b412-b3b7da3d830f");
            var Q2;
            Q2=sQuery(id+"F3.wireOp",EDGE,"b69f99c7-a6d0-4d1b-8752-9e82ab4c99ec");
            extrude(context, id + "F4", {"entities" : qUnion([Q0]), "operationType" : NewBodyOperationType.ADD, "surfaceEntities" : qUnion([Q1, Q2]), "depth" : 350 * mm});
        }
        {
            var Q0;
            Q0=makeQuery(id+"F4.opExtrude","SWEPT_BODY",BODY,{"disambiguationData":[OSD([sQuery(id+"F3.wireOp",EDGE,"15c6da4e-992d-4824-9d20-70d2d6be9970"),sQuery(id+"F3.wireOp",EDGE,"268c69ec-46be-456f-85eb-69decc32fe39"),sQuery(id+"F3.wireOp",EDGE,"1d386307-6059-4203-bca6-0c1cec3c82e1"),sQuery(id+"F3.wireOp",EDGE,"7d7c66d2-f869-427f-806b-ad436cacd60e"),sQuery(id+"F3.wireOp",EDGE,"1db91850-860e-493f-a3af-7a0f3f1512ae"),sQuery(id+"F3.wireOp",EDGE,"2c65f23b-9f03-4f6f-ab37-de452af29e3c"),sQuery(id+"F3.wireOp",EDGE,"ba006cbc-bbd7-44d9-84cc-9cde0967c280"),sQuery(id+"F3.wireOp",EDGE,"ae950208-c781-4a25-8fcf-ffe59b9085ff"),sQuery(id+"F3.wireOp",EDGE,"3cce0944-c62d-4831-9b9d-d1a418d328b4"),sQuery(id+"F3.wireOp",EDGE,"9edc5e7d-16c0-40c4-98ad-6b91d5df0e78"),sQuery(id+"F3.wireOp",EDGE,"aa452f44-44a2-4c64-bff5-a2a639df00db"),sQuery(id+"F3.wireOp",EDGE,"16259f99-ce20-4b7b-81e1-fa0909c03eb4"),sQuery(id+"F3.wireOp",EDGE,"79895566-a943-429d-b257-d76af3645bdf"),sQuery(id+"F3.wireOp",EDGE,"a85490ef-f17e-45c8-b92b-28215162778a"),sQuery(id+"F3.wireOp",EDGE,"322f1036-a6fd-4992-ab69-5919540af7a6"),sQuery(id+"F3.wireOp",EDGE,"0a87ff38-4ab4-4140-b3c3-2d7501d9f3b1"),sQuery(id+"F3.wireOp",EDGE,"a6e7bdf2-ef3e-49d4-9b3c-e34f5a41e0c4"),sQuery(id+"F3.wireOp",EDGE,"3e588790-576f-47c1-9730-f5e27fa1e8f9"),sQuery(id+"F3.wireOp",EDGE,"ce3739ef-15fd-4754-ad9c-ccf511a9a8fb"),sQuery(id+"F3.wireOp",EDGE,"201134a3-66f3-4a3f-aa9b-76948966efc0"),sQuery(id+"F3.wireOp",EDGE,"65b511ea-0759-428d-8070-88e1f521d8ea"),sQuery(id+"F3.wireOp",EDGE,"c37cddb6-5cf8-4891-aff4-7191a72080b9"),sQuery(id+"F3.wireOp",EDGE,"52a43dbd-e952-43e1-be3d-d70e107260e6"),sQuery(id+"F3.wireOp",EDGE,"08c1271f-f5c3-4f26-be27-7f5e21217dff"),sQuery(id+"F3.wireOp",EDGE,"59a09f58-0503-4180-962a-e04db21f0da8"),sQuery(id+"F3.wireOp",EDGE,"e56a4626-e956-42c3-bb5d-cd9dae1ca801"),sQuery(id+"F3.wireOp",EDGE,"5ff5d55f-af90-49eb-8040-353101557de8"),sQuery(id+"F3.wireOp",EDGE,"0ed7430b-e164-4f56-8af9-4534524aa7c0"),sQuery(id+"F3.wireOp",EDGE,"b5610a6e-b6bb-43e3-9a8d-d3d7c5f0098b"),sQuery(id+"F3.wireOp",EDGE,"1d417af8-88ad-47c2-a4e2-6fec82bd6695"),sQuery(id+"F3.wireOp",EDGE,"778ae99a-956a-4ddb-8078-d9bc57f9fc8e"),sQuery(id+"F3.wireOp",EDGE,"5b19af09-f144-446e-9dfa-8766819c9efd"),sQuery(id+"F3.wireOp",EDGE,"028339f6-0475-4a57-af8d-550e32ad7466"),sQuery(id+"F3.wireOp",EDGE,"d5ae35b6-d210-433a-92c8-e92622696872"),sQuery(id+"F3.wireOp",EDGE,"16a2e606-2caa-4876-9ffa-8f08c4ff3a37"),sQuery(id+"F3.wireOp",EDGE,"5b90b144-be56-4de7-a9dd-c1e0336acbe3"),sQuery(id+"F3.wireOp",EDGE,"5912d126-c5fc-41e4-bfb8-b4fefc52ca72"),sQuery(id+"F3.wireOp",EDGE,"2e96ce95-bd3e-4f27-a7f8-b62cf5efe954"),sQuery(id+"F3.wireOp",EDGE,"ecb4e259-1207-4dd0-bc3c-87c6506cc3a5"),sQuery(id+"F3.wireOp",EDGE,"105fb72e-4d79-4204-af2f-b3b26f5eb8d1"),sQuery(id+"F3.wireOp",EDGE,"fa59b598-df54-48c6-bb8f-c5f7618c69d0"),sQuery(id+"F3.wireOp",EDGE,"a6beef0d-f124-47ac-b957-e6cd3057a354"),sQuery(id+"F3.wireOp",EDGE,"7c3eaf53-dcb7-43b1-ad18-80ff953eb59e"),sQuery(id+"F3.wireOp",EDGE,"281fe206-104f-408f-94b6-be79f12604c9")])]});
            var Q1;
            Q1=makeQuery(id+"F4.opExtrude","SWEPT_BODY",BODY,{"disambiguationData":[OSD([sQuery(id+"F3.wireOp",EDGE,"58f6206a-5554-41d4-8cf7-6e0b4724a469"),sQuery(id+"F3.wireOp",EDGE,"85dabe77-b6aa-43d5-a519-64383616f71e"),sQuery(id+"F3.wireOp",EDGE,"4b679fe6-9e11-497d-b8fd-14ca14e49ddd"),sQuery(id+"F3.wireOp",EDGE,"51de25f6-d59e-4805-a327-1fd7e38869c8"),sQuery(id+"F3.wireOp",EDGE,"d47977fb-70d3-4df8-bc35-66fcc0e556e0"),sQuery(id+"F3.wireOp",EDGE,"235006b0-8f14-4ca2-82f0-f96b6b8c4766"),sQuery(id+"F3.wireOp",EDGE,"0fc7acd6-1c1d-47a8-ba12-62eb658d35ca"),sQuery(id+"F3.wireOp",EDGE,"883fa5e3-ca4c-4ce6-a249-4debf538fe24"),sQuery(id+"F3.wireOp",EDGE,"1da09ed1-22d9-43a1-a655-8acff5d61309"),sQuery(id+"F3.wireOp",EDGE,"32654a82-a09a-444f-bf73-45f818f0f235"),sQuery(id+"F3.wireOp",EDGE,"a398fd80-a0a9-4724-ba0e-1a7a000baa92"),sQuery(id+"F3.wireOp",EDGE,"f39f97c8-53f5-4046-9905-b28daecd4f10"),sQuery(id+"F3.wireOp",EDGE,"2484d883-0ec2-4c7d-9023-165ebbef226c"),sQuery(id+"F3.wireOp",EDGE,"f026d96f-3d32-4113-a1c9-3545f5cdbe4a"),sQuery(id+"F3.wireOp",EDGE,"974fee18-719e-4620-aace-d3676da2011b"),sQuery(id+"F3.wireOp",EDGE,"0c5766d2-a026-45af-bffd-0d1f783d5157"),sQuery(id+"F3.wireOp",EDGE,"5da13fee-9c04-45d8-805f-c7a03dde2383"),sQuery(id+"F3.wireOp",EDGE,"dbea32a3-85bd-4957-aef2-b6fe64a02f6b"),sQuery(id+"F3.wireOp",EDGE,"fba134ea-bf40-4191-ad8f-cc6b2b040a97"),sQuery(id+"F3.wireOp",EDGE,"0c19e200-7cd5-4fcb-83ed-261bd7936bc7"),sQuery(id+"F3.wireOp",EDGE,"246b843b-ea86-44e5-9cb9-335e6677b61d"),sQuery(id+"F3.wireOp",EDGE,"c1b3c9bc-1eb4-4c9b-99c8-0cebed89395a"),sQuery(id+"F3.wireOp",EDGE,"f93eebc3-1447-4029-8362-91325193ac2b"),sQuery(id+"F3.wireOp",EDGE,"bf86b12d-53a9-4c19-abaa-b1e658933ceb"),sQuery(id+"F3.wireOp",EDGE,"89646a71-1a60-4e14-b80a-74fb601d0855"),sQuery(id+"F3.wireOp",EDGE,"7b03dcde-0a52-4f3c-80e9-110d1d805e93"),sQuery(id+"F3.wireOp",EDGE,"83e8d1f3-8820-485b-8b6d-3ecd79124883"),sQuery(id+"F3.wireOp",EDGE,"ec7b56eb-ca95-44fd-a774-e9b7f9d3f50d"),sQuery(id+"F3.wireOp",EDGE,"31861aa6-cfd1-43ce-a7c5-bacfb7e2a30f"),sQuery(id+"F3.wireOp",EDGE,"fa3de647-1dd9-4141-982b-74ae8d07851d"),sQuery(id+"F3.wireOp",EDGE,"75d7c1c5-761c-4178-bfd4-4f469045899b"),sQuery(id+"F3.wireOp",EDGE,"4b3d7518-bd5d-4ecc-b2c5-d8dd665de4f4"),sQuery(id+"F3.wireOp",EDGE,"3be2682d-01bd-4f31-9cde-9df16a01e4a9"),sQuery(id+"F3.wireOp",EDGE,"72d3c7a9-2794-46eb-9b0d-6c526cc1b9a3"),sQuery(id+"F3.wireOp",EDGE,"0137e336-6b26-4f8d-b9ad-47ce1aa9eb31"),sQuery(id+"F3.wireOp",EDGE,"96000e4a-2d86-4b9f-af7d-a1c875cc048c"),sQuery(id+"F3.wireOp",EDGE,"139c5a79-9c0f-4e15-b57f-4c09662495a3"),sQuery(id+"F3.wireOp",EDGE,"8ea04d8b-b3da-46bb-9742-d8cba6b23bda"),sQuery(id+"F3.wireOp",EDGE,"b352b580-467e-481c-88ac-6217b8462947"),sQuery(id+"F3.wireOp",EDGE,"2503a493-1722-4539-8d54-7329fc0b116a"),sQuery(id+"F3.wireOp",EDGE,"a0615e06-0a48-4c65-8818-f0f693937022"),sQuery(id+"F3.wireOp",EDGE,"08389002-1ce8-438a-b5a4-698ca33590c2"),sQuery(id+"F3.wireOp",EDGE,"1756e4aa-c30a-461e-962c-81ee35d31e55"),sQuery(id+"F3.wireOp",EDGE,"5f84c249-07ea-4efb-9be3-ca494937f772"),sQuery(id+"F3.wireOp",EDGE,"cbefd041-b54f-4587-87b6-437b2290d1fc"),sQuery(id+"F3.wireOp",EDGE,"d44f58d4-f1a7-4aec-b016-8e7f1e498aeb"),sQuery(id+"F3.wireOp",EDGE,"0a5be90b-7545-44ea-9f2d-c726a5a2121c"),sQuery(id+"F3.wireOp",EDGE,"0cfaa442-d102-4580-8ef6-489f2aa1e6b3")])]});
            var Q2;
            Q2=makeQuery(id+"F4.opExtrude","SWEPT_BODY",BODY,{"disambiguationData":[OSD([sQuery(id+"F3.wireOp",EDGE,"9cc7aec6-4d94-4577-ab6c-32f5aa316238"),sQuery(id+"F3.wireOp",EDGE,"5ab2d840-4a32-405a-8c4b-a8126e3e1bc1"),sQuery(id+"F3.wireOp",EDGE,"56de48b4-9620-4637-8196-310e2641530f"),sQuery(id+"F3.wireOp",EDGE,"55327826-e64b-4830-85f2-3f22d36f43b5"),sQuery(id+"F3.wireOp",EDGE,"0245b46f-a639-4a95-8ca3-1568736ceed2"),sQuery(id+"F3.wireOp",EDGE,"9bd8a002-6ca7-4c84-8984-a620eefad103"),sQuery(id+"F3.wireOp",EDGE,"d4736c5e-da0b-46a0-ba9d-17ae07bb2b66"),sQuery(id+"F3.wireOp",EDGE,"125695b8-77e6-4e99-8f78-5f8fae1a0c71"),sQuery(id+"F3.wireOp",EDGE,"c9f25b10-a495-4684-8f25-8f255fabab6e"),sQuery(id+"F3.wireOp",EDGE,"0dbee67a-2ab6-4abb-ae16-0fe64d623848"),sQuery(id+"F3.wireOp",EDGE,"92c08d8e-ed2e-41a3-9c1a-b5ddaf8a0bf1"),sQuery(id+"F3.wireOp",EDGE,"00fabb15-0c1e-492e-85c1-17390e5b12bc"),sQuery(id+"F3.wireOp",EDGE,"065a9352-dddb-4e3f-b02a-444c867b75fe"),sQuery(id+"F3.wireOp",EDGE,"ef206bb6-e4f2-4189-9fc7-a7823c329ad6"),sQuery(id+"F3.wireOp",EDGE,"7199cbbe-c9bf-4cb9-b928-2ff8a84eb09e"),sQuery(id+"F3.wireOp",EDGE,"17bf9ed1-b881-4f74-816d-3511b6b328c7"),sQuery(id+"F3.wireOp",EDGE,"e5b615d0-4193-495d-b285-bd69ae30f000"),sQuery(id+"F3.wireOp",EDGE,"cfeaf62f-6be1-426b-9732-01e1a667be7e"),sQuery(id+"F3.wireOp",EDGE,"ac56344b-5ee6-4fa5-8e47-65b2a4ea3a01"),sQuery(id+"F3.wireOp",EDGE,"45b5fa53-15fd-43a0-91b0-943cc3286fc9")])]});
            var Q3;
            Q3=makeQuery(id+"F4.opExtrude","SWEPT_BODY",BODY,{"disambiguationData":[OSD([sQuery(id+"F3.wireOp",EDGE,"7bdfe37d-9957-4663-8239-5490fd3220d9"),sQuery(id+"F3.wireOp",EDGE,"6a91314f-c002-4565-bbf8-bb9f29165fb8"),sQuery(id+"F3.wireOp",EDGE,"b69f99c7-a6d0-4d1b-8752-9e82ab4c99ec"),sQuery(id+"F3.wireOp",EDGE,"c928f899-12af-4b01-b412-b3b7da3d830f"),sQuery(id+"F3.wireOp",EDGE,"ffa58721-cdd5-406d-be26-d96f7a050df4"),sQuery(id+"F3.wireOp",EDGE,"02fc7fb8-293b-44ff-ab78-63506d0aedb9"),sQuery(id+"F3.wireOp",EDGE,"147fb6cb-2565-4fb5-9280-6afbf9eef36b"),sQuery(id+"F3.wireOp",EDGE,"2cee3704-4124-415a-b391-31af1cf305d7"),sQuery(id+"F3.wireOp",EDGE,"32b2fb71-03c8-4978-9d95-2b5aaf044d0d"),sQuery(id+"F3.wireOp",EDGE,"e5d05796-7d6c-4350-8a4e-d55f5ade2f77"),sQuery(id+"F3.wireOp",EDGE,"77b1164c-8dd4-4680-b616-ac151a422eb2"),sQuery(id+"F3.wireOp",EDGE,"ec0798b8-0fbb-49ea-9766-39d2ee0936b0"),sQuery(id+"F3.wireOp",EDGE,"c4af6478-2a03-47a6-862f-c0c71886b8a3"),sQuery(id+"F3.wireOp",EDGE,"1912a38f-fa28-45c6-ab33-84cac2787056"),sQuery(id+"F3.wireOp",EDGE,"5d79fa95-f66d-4d2b-923b-4d54735f1fbd"),sQuery(id+"F3.wireOp",EDGE,"2db7aef4-a710-4bcf-9c1c-a8a87719953d"),sQuery(id+"F3.wireOp",EDGE,"183449de-345c-4115-9bca-43a403e62dbd"),sQuery(id+"F3.wireOp",EDGE,"e3ac8c9b-cab5-44b0-ad81-0e2b680c384a"),sQuery(id+"F3.wireOp",EDGE,"92e85db6-f458-41f6-a9a1-1e1a1a7e7809"),sQuery(id+"F3.wireOp",EDGE,"f0dbb46f-43a9-447b-9c75-8dfc9b95470d"),sQuery(id+"F3.wireOp",EDGE,"4b73f5f6-f769-4414-bdba-7d253e58fff4"),sQuery(id+"F3.wireOp",EDGE,"a88669dc-35b3-46bb-964f-c9bf6c4ab898"),sQuery(id+"F3.wireOp",EDGE,"2c559bae-f38f-4377-91e6-3c9de70acf11"),sQuery(id+"F3.wireOp",EDGE,"c1caf99b-adaa-42fe-a319-8cbcd819cf89"),sQuery(id+"F3.wireOp",EDGE,"54b04dd4-0ec4-4956-b19c-1141095738e3"),sQuery(id+"F3.wireOp",EDGE,"098f7a84-b7b8-4879-b21a-5c38879e4110"),sQuery(id+"F3.wireOp",EDGE,"b406a8e6-a226-4f3d-ac30-e4d06e4dac62"),sQuery(id+"F3.wireOp",EDGE,"36f95d1d-68ce-4231-ad71-3960c85e5915"),sQuery(id+"F3.wireOp",EDGE,"dc12cad8-2eed-454e-aa74-30099b1c9064"),sQuery(id+"F3.wireOp",EDGE,"4c78a4fd-cd81-43d6-85d6-6e4d3fbc1e98"),sQuery(id+"F3.wireOp",EDGE,"ee9e30de-787b-4e8f-b425-43a8e9289f81"),sQuery(id+"F3.wireOp",EDGE,"2518a3a4-c96b-4463-8704-0b71c65c60d2"),sQuery(id+"F3.wireOp",EDGE,"c9129a67-398c-4e37-92cb-2d54ff2e2e82"),sQuery(id+"F3.wireOp",EDGE,"d429d547-9f5b-42c6-bcca-effad2fa908f"),sQuery(id+"F3.wireOp",EDGE,"99d16e94-b2b3-43d5-9c7b-7bd463994dcb"),sQuery(id+"F3.wireOp",EDGE,"32993909-9a70-47ee-9097-89fff220f839"),sQuery(id+"F3.wireOp",EDGE,"6eabbeed-9496-4825-b168-63782a34f495"),sQuery(id+"F3.wireOp",EDGE,"f74987e3-8e60-4a5b-857f-839ae8aaf0cf"),sQuery(id+"F3.wireOp",EDGE,"1c218c86-035d-4441-93c0-9621d3297c3a"),sQuery(id+"F3.wireOp",EDGE,"0133f513-4b11-4cc4-b075-4625e9591e41"),sQuery(id+"F3.wireOp",EDGE,"fe921ad4-a8f5-4772-9aeb-350aca2e8948"),sQuery(id+"F3.wireOp",EDGE,"bfde0a4f-3cec-4f8e-8a23-dd1441b34c2b"),sQuery(id+"F3.wireOp",EDGE,"b41521ff-c5df-4b64-83ed-5e7635cf4438"),sQuery(id+"F3.wireOp",EDGE,"ed692599-6bbb-4379-8e89-ea326a0a0f87"),sQuery(id+"F3.wireOp",EDGE,"a98451c0-d76c-436e-99f9-a3fe9c8430a4"),sQuery(id+"F3.wireOp",EDGE,"561965b2-3050-4f49-9305-d98a2b852bbe"),sQuery(id+"F3.wireOp",EDGE,"e13dfa59-48e6-4b4e-94b9-1fc5254b0f2e"),sQuery(id+"F3.wireOp",EDGE,"0354e106-253a-4bfa-b5b7-b09cd0f2f6c0"),sQuery(id+"F3.wireOp",EDGE,"8df1dcc8-d00a-4777-85fd-8af8e9830bd1"),sQuery(id+"F3.wireOp",EDGE,"26ce3762-0d1a-4b81-9a23-debcfc24da1c"),sQuery(id+"F3.wireOp",EDGE,"3e900f8f-3ffb-4e32-b536-61fea2f3e30a"),sQuery(id+"F3.wireOp",EDGE,"4a1b5445-5559-461f-b6f1-b4cd9b95ea10")])]});
            var Q4;
            Q4=makeQuery(id+"F1.opRevolve","SWEPT_BODY",BODY,{"disambiguationData":[OSD([sQuery(id+"F0.wireOp",EDGE,"E0"),sQuery(id+"F0.wireOp",EDGE,"E1")])]});
            var Q5;
            Q5=qCreatedBy(makeId("Origin.pointOp"),VERTEX);
            transform(context, id + "F5", {"entities" : qUnion([Q0, Q1, Q2, Q3, Q4]), "transformType" : TransformType.SCALE_UNIFORMLY, "scale" : 0.03, "scalePoint" : qUnion([Q5]), "makeCopy" : false});
        }
        {
            var Q0;
            Q0=qCreatedBy(makeId("Top.planeOp"),FACE);
            var sketch = newSketch(context, id + "F6", { "sketchPlane" : qUnion([Q0])});
            skLineSegment(sketch, "E544", {"start": v(0, 15) * mm, "end": v(0, -15) * mm});
            skArc(sketch, "E545", {"start": v(0, 15) * mm, "mid": v(-15, 0) * mm, "end": v(0, -15) * mm});
            skArc(sketch, "E546", {"start": v(0, 10.25) * mm, "mid": v(-10.25, 0) * mm, "end": v(0, -10.25) * mm});
            skArc(sketch, "E547", {"start": v(0, 7) * mm, "mid": v(-7, 0) * mm, "end": v(0, -7) * mm});
            skSolve(sketch);
        }
        {
            var Q0;
            {var subQ0=sQuery(id+"F6.wireOp",EDGE,"E545");Q0=makeQuery(id+"F6.imprint","IMPRINT",FACE,{"disambiguationData":[TD([[makeQuery(id+"F6.imprint","IMPRINT",EDGE,{"derivedFrom":subQ0}),1.0]])]});}
            var Q1;
            {var subQ0=sQuery(id+"F6.wireOp",EDGE,"E547");Q1=makeQuery(id+"F6.imprint","IMPRINT",FACE,{"disambiguationData":[TD([[makeQuery(id+"F6.imprint","IMPRINT",EDGE,{"derivedFrom":subQ0}),1.0]])]});}
            var Q2;
            Q2=sQuery(id+"F6.wireOp",EDGE,"E544");
            revolve(context, id + "F7", {"operationType" : NewBodyOperationType.REMOVE, "entities" : qUnion([Q0, Q1]), "axis" : qUnion([Q2]), "revolveType" : RevolveType.FULL});
        }
        {
            var Q0;
            Q0=makeQuery(id+"F1.opRevolve","SWEPT_BODY",BODY,{"disambiguationData":[OSD([sQuery(id+"F0.wireOp",EDGE,"E0"),sQuery(id+"F0.wireOp",EDGE,"E1")])]});
            var Q1;
            Q1=sQuery(id+"F0.wireOp",VERTEX,"E1.center");
            transform(context, id + "F8", {"entities" : qUnion([Q0]), "transformType" : TransformType.SCALE_UNIFORMLY, "scale" : 1.4, "scalePoint" : qUnion([Q1]), "makeCopy" : false});
        }
        {
            var Q0;
            Q0=qCreatedBy(makeId("Front.planeOp"),FACE);
            var sketch = newSketch(context, id + "F9", { "sketchPlane" : qUnion([Q0])});
            skCircle(sketch, "E548", {"center": v(0, -5.12) * mm, "radius": 2 * mm});
            skSolve(sketch);
        }
        {
            var Q0;
            Q0=qSketchRegion(id+"F9",true);
            extrude(context, id + "F10", {"entities" : qUnion([Q0]), "operationType" : NewBodyOperationType.REMOVE, "oppositeDirection" : true, "depth" : 25 * mm});
        }
    });
